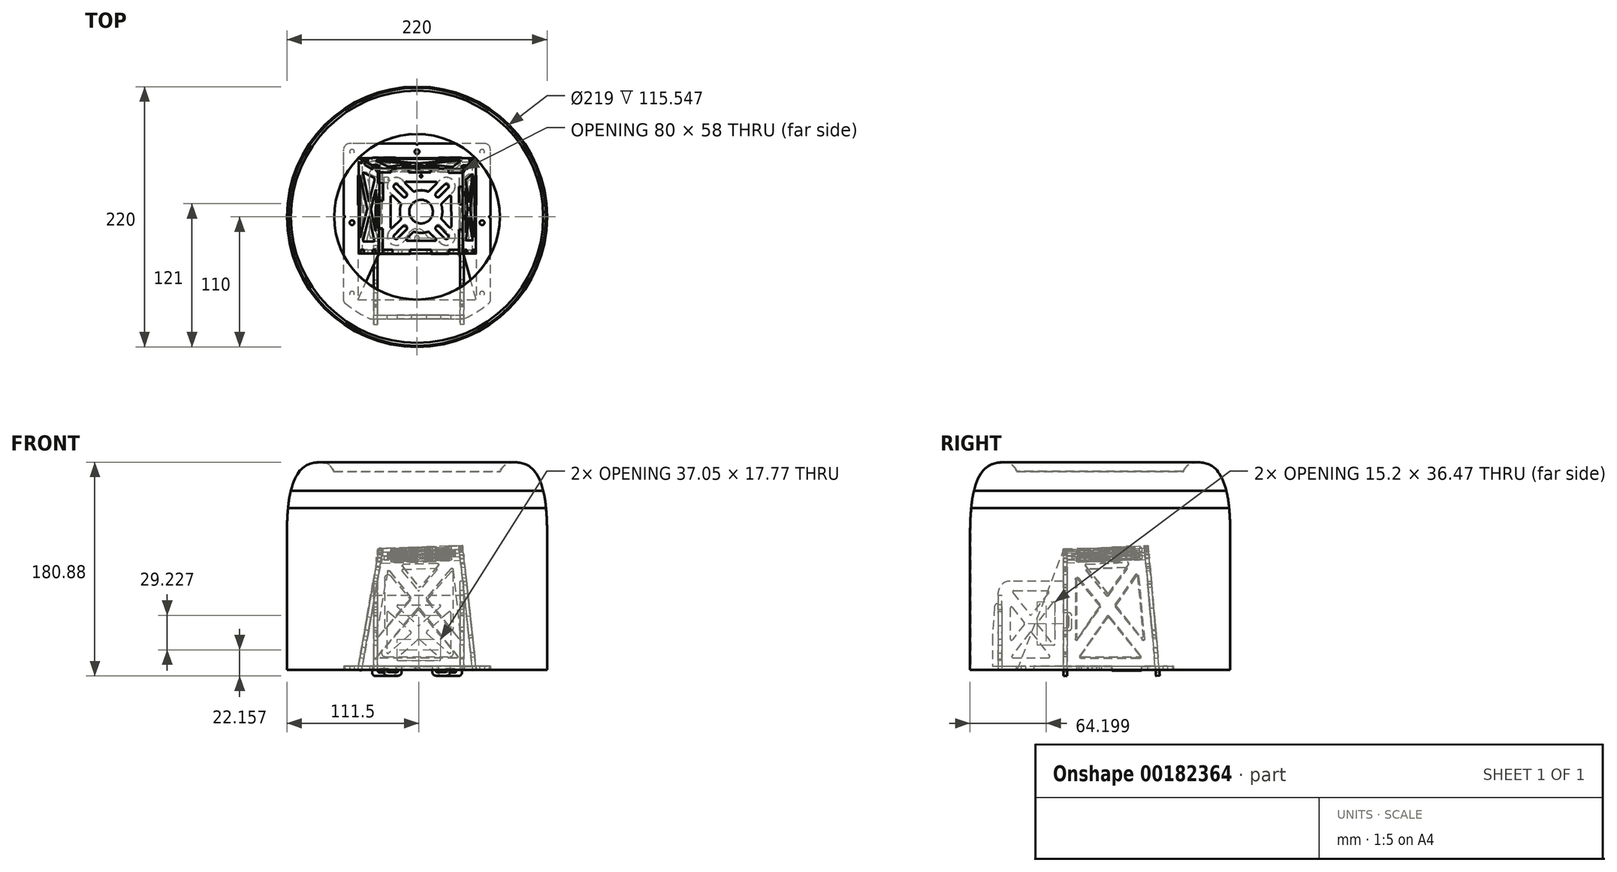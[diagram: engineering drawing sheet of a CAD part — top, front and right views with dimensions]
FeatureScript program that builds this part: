
annotation { "Feature Type Name" : "Feature", "Feature Type Description" : "" }
export const myFeature = defineFeature(function(context is Context, id is Id, definition is map)
    precondition{}
    {
        {
            var Q0;
            Q0=qCreatedBy(makeId("Top.planeOp"),FACE);
            var sketch = newSketch(context, id + "F0", { "sketchPlane" : qUnion([Q0])});
            skLineSegment(sketch, "E0.bottom", {"start": v(-50, 50) * mm, "end": v(50, 50) * mm});
            skLineSegment(sketch, "E0.top", {"start": v(-50, -70) * mm, "end": v(50, -70) * mm});
            skLineSegment(sketch, "E0.left", {"start": v(-50, 50) * mm, "end": v(-50, -70) * mm});
            skLineSegment(sketch, "E0.right", {"start": v(50, 50) * mm, "end": v(50, -70) * mm});
            skSolve(sketch);
        }
        {
            var Q0;
            Q0=qCreatedBy(makeId("Top.planeOp"),FACE);
            cPlane(context, id + "F1", {"entities" : qUnion([Q0]), "cplaneType" : CPlaneType.OFFSET, "offset" : 105 * mm, "width" : 150 * mm, "height" : 150 * mm});
        }
        {
            var Q0;
            Q0=qCreatedBy(id+"F1.planeOp",FACE);
            var sketch = newSketch(context, id + "F2", { "sketchPlane" : qUnion([Q0])});
            skLineSegment(sketch, "E1.bottom", {"start": v(-31.5, 40.5) * mm, "end": v(38.5, 40.5) * mm});
            skLineSegment(sketch, "E1.top", {"start": v(-31.5, -29.5) * mm, "end": v(38.5, -29.5) * mm});
            skLineSegment(sketch, "E1.left", {"start": v(-31.5, 40.5) * mm, "end": v(-31.5, -29.5) * mm});
            skLineSegment(sketch, "E1.right", {"start": v(38.5, 40.5) * mm, "end": v(38.5, -29.5) * mm});
            skSolve(sketch);
        }
        {
            var Q0;
            Q0 = qSketchRegion(id + "F0", true);
            var Q1;
            Q1 = qSketchRegion(id + "F2", true);
            loft(context, id + "F3", {"sheetProfilesArray" : [{ "sheetProfileEntities" : qUnion([Q0]) }, { "sheetProfileEntities" : qUnion([Q1]) }]});
        }
        {
            var Q0;
            Q0=qCreatedBy(id+"F1.planeOp",FACE);
            var sketch = newSketch(context, id + "F4", { "sketchPlane" : qUnion([Q0])});
            skLineSegment(sketch, "E2", {"start": v(-55.6, 40.5) * mm, "end": v(63.29, 40.5) * mm});
            skSolve(sketch);
        }
        {
            var Q0;
            Q0=sQuery(id+"F4.wireOp",EDGE,"E2");
            var Q1;
            Q1=qCreatedBy(id+"F1.planeOp",FACE);
            cPlane(context, id + "F5", {"entities" : qUnion([Q0, Q1]), "cplaneType" : CPlaneType.LINE_ANGLE, "offset" : 25 * mm, "angle" : 2.5 * degree, "width" : 150 * mm, "height" : 150 * mm});
        }
        {
            var Q0;
            Q0=qCreatedBy(id+"F5.planeOp",FACE);
            var sketch = newSketch(context, id + "F6", { "sketchPlane" : qUnion([Q0])});
            skLineSegment(sketch, "E3", {"start": v(38.5, -42.4) * mm, "end": v(38.5, 44.3) * mm});
            skSolve(sketch);
        }
        {
            var Q0;
            Q0=qCreatedBy(id+"F5.planeOp",FACE);
            var Q1;
            Q1=sQuery(id+"F6.wireOp",EDGE,"E3");
            cPlane(context, id + "F7", {"entities" : qUnion([Q0, Q1]), "cplaneType" : CPlaneType.LINE_ANGLE, "offset" : 25 * mm, "angle" : 2 * degree, "width" : 150 * mm, "height" : 150 * mm});
        }
        {
            var Q0;
            Q0=qCreatedBy(id+"F7.planeOp",FACE);
            cPlane(context, id + "F8", {"entities" : qUnion([Q0]), "cplaneType" : CPlaneType.OFFSET, "offset" : 6.2 * mm, "oppositeDirection" : true, "width" : 150 * mm, "height" : 150 * mm});
        }
        {
            var Q0;
            Q0=qCreatedBy(id+"F7.planeOp",FACE);
            var sketch = newSketch(context, id + "F9", { "sketchPlane" : qUnion([Q0])});
            skLineSegment(sketch, "E4", {"start": v(-28.4, 45.16) * mm, "end": v(-28.96, -27.3) * mm});
            skLineSegment(sketch, "E5", {"start": v(42.08, 45.04) * mm, "end": v(-28.4, 45.16) * mm});
            skLineSegment(sketch, "E6", {"start": v(42.42, -26.22) * mm, "end": v(42.08, 45.04) * mm});
            skLineSegment(sketch, "E7", {"start": v(-28.96, -27.3) * mm, "end": v(42.42, -26.22) * mm});
            skSolve(sketch);
        }
        {
            var Q1;
            Q1 = qSketchRegion(id + "F9", true);
            var Q2;
            Q2 = qSketchRegion(id + "F2", true);
            loft(context, id + "F10", {"operationType" : NewBodyOperationType.REMOVE, "sheetProfilesArray" : [{ "sheetProfileEntities" : qUnion([Q1]) }, { "sheetProfileEntities" : qUnion([Q2]) }]});
        }
        {
            var Q0;
            Q0=qCreatedBy(makeId("Top.planeOp"),FACE);
            var sketch = newSketch(context, id + "F11", { "sketchPlane" : qUnion([Q0])});
            skLineSegment(sketch, "E8.0.0", {"start": v(-50, -55) * mm, "end": v(-50, -40) * mm, "construction": true});
            skLineSegment(sketch, "E8.0.1", {"start": v(38, 50) * mm, "end": v(18, 50) * mm});
            skLineSegment(sketch, "E8.0.2", {"start": v(50, -55) * mm, "end": v(50, -40) * mm, "construction": true});
            skLineSegment(sketch, "E9.0", {"start": v(-62, -71.06) * mm, "end": v(-62, -1) * mm});
            skLineSegment(sketch, "E9.2", {"start": v(62, -71.06) * mm, "end": v(62, -1) * mm});
            skLineSegment(sketch, "E9.3", {"start": v(57, 62) * mm, "end": v(1, 62) * mm});
            skLineSegment(sketch, "E10.0", {"start": v(-46.8, -55) * mm, "end": v(-46.8, -40) * mm, "construction": true});
            skLineSegment(sketch, "E10.2", {"start": v(46.8, -55) * mm, "end": v(46.8, -40) * mm, "construction": true});
            skLineSegment(sketch, "E10.3", {"start": v(38, 46.8) * mm, "end": v(18, 46.8) * mm});
            skLineSegment(sketch, "E11.0", {"start": v(-40, -15.5) * mm, "end": v(-40, 37.5) * mm});
            skLineSegment(sketch, "E11.2", {"start": v(40, -15.5) * mm, "end": v(40, 37.5) * mm});
            skLineSegment(sketch, "E11.3", {"start": v(37.5, 40) * mm, "end": v(-37.5, 40) * mm});
            skPoint(sketch, "E12.visualSharp", {"position": v(40, 40) * mm});
            skArc(sketch, "E12.filletArc", {"start": v(40, 37.5) * mm, "mid": v(39.27, 39.27) * mm, "end": v(37.5, 40) * mm});
            skPoint(sketch, "E13.visualSharp", {"position": v(-40, 40) * mm});
            skArc(sketch, "E13.filletArc", {"start": v(-37.5, 40) * mm, "mid": v(-39.27, 39.27) * mm, "end": v(-40, 37.5) * mm});
            skLineSegment(sketch, "E14.0", {"start": v(50, -55) * mm, "end": v(46.8, -55) * mm, "construction": true});
            skLineSegment(sketch, "E15.0", {"start": v(50, -40) * mm, "end": v(46.8, -40) * mm, "construction": true});
            skLineSegment(sketch, "E16.0", {"start": v(50, 35) * mm, "end": v(46.8, 35) * mm});
            skLineSegment(sketch, "E17.0", {"start": v(50, 10) * mm, "end": v(46.8, 10) * mm});
            skLineSegment(sketch, "E18.trimOffspring", {"start": v(-46.8, -40) * mm, "end": v(-50, -40) * mm, "construction": true});
            skLineSegment(sketch, "E19.trimOffspring", {"start": v(-46.8, 35) * mm, "end": v(-50, 35) * mm});
            skLineSegment(sketch, "E20.trimOffspring", {"start": v(-46.8, 10) * mm, "end": v(-50, 10) * mm});
            skLineSegment(sketch, "E21.trimOffspring", {"start": v(-46.8, -55) * mm, "end": v(-50, -55) * mm, "construction": true});
            skLineSegment(sketch, "E22.trimOffspring", {"start": v(-18, 46.8) * mm, "end": v(-18, 50) * mm});
            skLineSegment(sketch, "E23.trimOffspring", {"start": v(-38, 46.8) * mm, "end": v(-38, 50) * mm});
            skLineSegment(sketch, "E24.trimOffspring", {"start": v(18, 46.8) * mm, "end": v(18, 50) * mm});
            skLineSegment(sketch, "E25.trimOffspring", {"start": v(50, 10) * mm, "end": v(50, 35) * mm});
            skLineSegment(sketch, "E26.trimOffspring", {"start": v(46.8, 10) * mm, "end": v(46.8, 35) * mm});
            skLineSegment(sketch, "E27.trimOffspring", {"start": v(38, 46.8) * mm, "end": v(38, 50) * mm});
            skLineSegment(sketch, "E28.trimOffspring", {"start": v(-18, 46.8) * mm, "end": v(-38, 46.8) * mm});
            skLineSegment(sketch, "E29.trimOffspring", {"start": v(-18, 50) * mm, "end": v(-38, 50) * mm});
            skLineSegment(sketch, "E30.trimOffspring", {"start": v(-50, 10) * mm, "end": v(-50, 35) * mm});
            skLineSegment(sketch, "E31.trimOffspring", {"start": v(-46.8, 10) * mm, "end": v(-46.8, 35) * mm});
            skPoint(sketch, "E32.visualSharp", {"position": v(62, 62) * mm});
            skArc(sketch, "E32.filletArc", {"start": v(62, 57) * mm, "mid": v(60.54, 60.54) * mm, "end": v(57, 62) * mm});
            skPoint(sketch, "E33.visualSharp", {"position": v(-62, 62) * mm});
            skArc(sketch, "E33.filletArc", {"start": v(-57, 62) * mm, "mid": v(-60.54, 60.54) * mm, "end": v(-62, 57) * mm});
            skLineSegment(sketch, "E34", {"start": v(-28, -28) * mm, "end": v(-13, -28) * mm});
            skLineSegment(sketch, "E35.0", {"start": v(-37.5, -18) * mm, "end": v(-12, -18) * mm});
            skLineSegment(sketch, "E36", {"start": v(-28, -28) * mm, "end": v(-28, -31.2) * mm});
            skLineSegment(sketch, "E37", {"start": v(-13, -28) * mm, "end": v(-13, -31.2) * mm});
            skLineSegment(sketch, "E38", {"start": v(13, -28) * mm, "end": v(13, -31.2) * mm});
            skLineSegment(sketch, "E39", {"start": v(28, -28) * mm, "end": v(28, -31.2) * mm});
            skLineSegment(sketch, "E40.trimOffspring", {"start": v(13, -28) * mm, "end": v(28, -28) * mm});
            skPoint(sketch, "E41.visualSharp", {"position": v(-40, -18) * mm});
            skArc(sketch, "E41.filletArc", {"start": v(-40, -15.5) * mm, "mid": v(-39.27, -17.27) * mm, "end": v(-37.5, -18) * mm});
            skPoint(sketch, "E42.visualSharp", {"position": v(40, -18) * mm});
            skArc(sketch, "E42.filletArc", {"start": v(37.5, -18) * mm, "mid": v(39.27, -17.27) * mm, "end": v(40, -15.5) * mm});
            skLineSegment(sketch, "E43.top", {"start": v(-28.5, -31.2) * mm, "end": v(-28, -31.2) * mm});
            skLineSegment(sketch, "E43.left", {"start": v(-33.5, -86.2) * mm, "end": v(-33.5, -71.2) * mm});
            skLineSegment(sketch, "E43.right", {"start": v(36.5, -86.2) * mm, "end": v(36.5, -71.2) * mm});
            skPoint(sketch, "E44.visualSharp", {"position": v(-33.5, -31.2) * mm});
            skArc(sketch, "E44.filletArc", {"start": v(-28.5, -31.2) * mm, "mid": v(-32.04, -32.66) * mm, "end": v(-33.5, -36.2) * mm});
            skPoint(sketch, "E45.visualSharp", {"position": v(36.5, -31.2) * mm});
            skArc(sketch, "E45.filletArc", {"start": v(36.5, -36.2) * mm, "mid": v(35.04, -32.66) * mm, "end": v(31.5, -31.2) * mm});
            skLineSegment(sketch, "E46.trimOffspring", {"start": v(-13, -31.2) * mm, "end": v(13, -31.2) * mm});
            skLineSegment(sketch, "E47.trimOffspring", {"start": v(28, -31.2) * mm, "end": v(31.5, -31.2) * mm});
            skLineSegment(sketch, "E48.0", {"start": v(-36.7, -71.2) * mm, "end": v(-36.7, -56.2) * mm});
            skLineSegment(sketch, "E49.0", {"start": v(39.7, -71.2) * mm, "end": v(39.7, -56.2) * mm});
            skLineSegment(sketch, "E50", {"start": v(-36.7, -56.2) * mm, "end": v(-33.5, -56.2) * mm});
            skLineSegment(sketch, "E51", {"start": v(-36.7, -71.2) * mm, "end": v(-33.5, -71.2) * mm});
            skLineSegment(sketch, "E52", {"start": v(36.5, -56.2) * mm, "end": v(39.7, -56.2) * mm});
            skLineSegment(sketch, "E53", {"start": v(36.5, -71.2) * mm, "end": v(39.7, -71.2) * mm});
            skLineSegment(sketch, "E54.trimOffspring", {"start": v(-33.5, -56.2) * mm, "end": v(-33.5, -36.2) * mm});
            skLineSegment(sketch, "E55.trimOffspring", {"start": v(36.5, -56.2) * mm, "end": v(36.5, -36.2) * mm});
            skLineSegment(sketch, "E56", {"start": v(-39.49, -86.2) * mm, "end": v(-33.5, -86.2) * mm});
            skLineSegment(sketch, "E57.trimOffspring", {"start": v(36.5, -86.2) * mm, "end": v(39.49, -86.2) * mm});
            skPoint(sketch, "E58.visualSharp", {"position": v(-62, -86.2) * mm});
            skPoint(sketch, "E59.visualSharp", {"position": v(62, -86.2) * mm});
            skArc(sketch, "E60", {"start": v(40.34, -86.01) * mm, "mid": v(51.26, -79.99) * mm, "end": v(61.3, -72.58) * mm});
            skArc(sketch, "E61.trimOffspring", {"start": v(-61.3, -72.58) * mm, "mid": v(-51.26, -79.99) * mm, "end": v(-40.34, -86.01) * mm});
            skPoint(sketch, "E62.visualSharp", {"position": v(62, -71.98) * mm});
            skArc(sketch, "E62.filletArc", {"start": v(61.3, -72.58) * mm, "mid": v(61.81, -71.9) * mm, "end": v(62, -71.06) * mm});
            skPoint(sketch, "E63.visualSharp", {"position": v(39.93, -86.2) * mm});
            skArc(sketch, "E63.filletArc", {"start": v(39.49, -86.2) * mm, "mid": v(39.92, -86.15) * mm, "end": v(40.34, -86.01) * mm});
            skPoint(sketch, "E64.visualSharp", {"position": v(-39.93, -86.2) * mm});
            skArc(sketch, "E64.filletArc", {"start": v(-40.34, -86.01) * mm, "mid": v(-39.92, -86.15) * mm, "end": v(-39.49, -86.2) * mm});
            skPoint(sketch, "E65.visualSharp", {"position": v(-62, -71.98) * mm});
            skArc(sketch, "E65.filletArc", {"start": v(-62, -71.06) * mm, "mid": v(-61.81, -71.9) * mm, "end": v(-61.3, -72.58) * mm});
            skCircle(sketch, "E66", {"center": v(-55, 55) * mm, "radius": 2 * mm});
            skCircle(sketch, "E67", {"center": v(55, 55) * mm, "radius": 2 * mm});
            skCircle(sketch, "E68", {"center": v(-55, -5) * mm, "radius": 2 * mm});
            skCircle(sketch, "E69", {"center": v(55, -5) * mm, "radius": 2 * mm});
            skCircle(sketch, "E70", {"center": v(-55, -65) * mm, "radius": 2 * mm});
            skCircle(sketch, "E71", {"center": v(55, -65) * mm, "radius": 2 * mm});
            skCircle(sketch, "E72", {"center": v(0, 55) * mm, "radius": 2 * mm});
            skCircle(sketch, "E73", {"center": v(0, -18) * mm, "radius": 2 * mm});
            skPoint(sketch, "E73.centerSnap0", {"position": v(0, -18) * mm});
            skArc(sketch, "E74", {"start": v(-7.38, -14.92) * mm, "mid": v(-4.84, -11.63) * mm, "end": v(-1, -10.06) * mm});
            skLineSegment(sketch, "E75.trimOffspring", {"start": v(12, -18) * mm, "end": v(37.5, -18) * mm});
            skPoint(sketch, "E76.visualSharp", {"position": v(8, -18) * mm});
            skArc(sketch, "E76.filletArc", {"start": v(7.38, -14.92) * mm, "mid": v(9.23, -17.16) * mm, "end": v(12, -18) * mm});
            skPoint(sketch, "E77.visualSharp", {"position": v(-8, -18) * mm});
            skArc(sketch, "E77.filletArc", {"start": v(-12, -18) * mm, "mid": v(-9.23, -17.16) * mm, "end": v(-7.38, -14.92) * mm});
            skLineSegment(sketch, "E78", {"start": v(0, 76.35) * mm, "end": v(0, -96.17) * mm, "construction": true});
            skPoint(sketch, "E78.startSnap0", {"position": v(0, 62) * mm});
            skLineSegment(sketch, "E79", {"start": v(102.81, 0) * mm, "end": v(-83.24, 0) * mm, "construction": true});
            skArc(sketch, "E80", {"start": v(-1, 62) * mm, "mid": v(0, 61) * mm, "end": v(1, 62) * mm});
            skLineSegment(sketch, "E81.trimOffspring", {"start": v(-1, 62) * mm, "end": v(-57, 62) * mm});
            skArc(sketch, "E82", {"start": v(-62, -1) * mm, "mid": v(-61, 0) * mm, "end": v(-62, 1) * mm});
            skLineSegment(sketch, "E83.trimOffspring", {"start": v(-62, 1) * mm, "end": v(-62, 57) * mm});
            skArc(sketch, "E84", {"start": v(62, 1) * mm, "mid": v(61, 0) * mm, "end": v(62, -1) * mm});
            skLineSegment(sketch, "E85.trimOffspring", {"start": v(62, 1) * mm, "end": v(62, 57) * mm});
            skArc(sketch, "E86", {"start": v(-1, -10.06) * mm, "mid": v(0, -11) * mm, "end": v(1, -10.06) * mm});
            skArc(sketch, "E87.trimOffspring", {"start": v(1, -10.06) * mm, "mid": v(4.84, -11.63) * mm, "end": v(7.38, -14.92) * mm});
            skArc(sketch, "E88", {"start": v(1, -10.06) * mm, "mid": v(0, -10) * mm, "end": v(-1, -10.06) * mm, "construction": true});
            skSolve(sketch);
        }
        {
            var Q0;
            Q0 = qSketchRegion(id + "F11", true);
            extrude(context, id + "F12", {"entities" : qUnion([Q0]), "depth" : 3.2 * mm});
        }
        {
            var Q0;
            Q0=sQuery(id+"F11.wireOp",EDGE,"E46.trimOffspring");
            cPlane(context, id + "F13", {"entities" : qUnion([Q0]), "cplaneType" : CPlaneType.LINE_ANGLE, "offset" : 25 * mm, "angle" : 0 * degree, "oppositeDirection" : true, "width" : 150 * mm, "height" : 150 * mm});
        }
        {
            var Q0;
            Q0=qCreatedBy(id+"F8.planeOp",FACE);
            var sketch = newSketch(context, id + "F14", { "sketchPlane" : qUnion([Q0])});
            skLineSegment(sketch, "E89", {"start": v(-3.3, -27.07) * mm, "end": v(11.7, -27.04) * mm});
            skPoint(sketch, "E90.orphan", {"position": v(-30.3, -30.03) * mm});
            skPoint(sketch, "E91.orphan", {"position": v(42.89, -28.92) * mm});
            skLineSegment(sketch, "E92.0", {"start": v(-27.02, -23.87) * mm, "end": v(-3.3, -23.84) * mm});
            skLineSegment(sketch, "E92.1", {"start": v(-26.5, 42.21) * mm, "end": v(-26.68, 20.42) * mm});
            skLineSegment(sketch, "E92.2", {"start": v(39.32, 42.1) * mm, "end": v(13.3, 42.15) * mm});
            skLineSegment(sketch, "E92.3", {"start": v(39.63, -23.77) * mm, "end": v(39.5, 3.31) * mm});
            skLineSegment(sketch, "E93", {"start": v(13.3, 45.88) * mm, "end": v(13.3, 42.15) * mm});
            skLineSegment(sketch, "E94", {"start": v(-30.98, 20.46) * mm, "end": v(-26.68, 20.42) * mm});
            skLineSegment(sketch, "E95", {"start": v(-31.1, 5.46) * mm, "end": v(-26.8, 5.42) * mm});
            skLineSegment(sketch, "E96", {"start": v(42.66, 18.33) * mm, "end": v(39.43, 18.31) * mm});
            skLineSegment(sketch, "E97", {"start": v(42.73, 3.33) * mm, "end": v(39.5, 3.31) * mm});
            skLineSegment(sketch, "E98", {"start": v(-3.3, -27.07) * mm, "end": v(-3.3, -23.84) * mm});
            skLineSegment(sketch, "E99", {"start": v(11.7, -27.04) * mm, "end": v(11.7, -23.81) * mm});
            skLineSegment(sketch, "E100.trimOffspring", {"start": v(-1.7, 42.17) * mm, "end": v(-26.5, 42.21) * mm});
            skLineSegment(sketch, "E101.trimOffspring", {"start": v(-26.8, 5.42) * mm, "end": v(-27.02, -23.87) * mm});
            skLineSegment(sketch, "E102.trimOffspring", {"start": v(11.7, -23.81) * mm, "end": v(39.63, -23.77) * mm});
            skLineSegment(sketch, "E103.trimOffspring", {"start": v(39.43, 18.31) * mm, "end": v(39.32, 42.1) * mm});
            skPoint(sketch, "E104.orphan", {"position": v(42.53, 45.33) * mm});
            skPoint(sketch, "E105.orphan", {"position": v(-29.71, 45.45) * mm});
            skPoint(sketch, "E106.orphan", {"position": v(-30.3, -27.1) * mm});
            skArc(sketch, "E107.0", {"start": v(19.26, 24.85) * mm, "mid": v(19.27, 21.17) * mm, "end": v(22.95, 21.18) * mm});
            skLineSegment(sketch, "E108.0", {"start": v(22.95, 21.18) * mm, "end": v(30, 28.27) * mm});
            skArc(sketch, "E109.0", {"start": v(30, 28.27) * mm, "mid": v(30, 31.94) * mm, "end": v(26.31, 31.94) * mm});
            skLineSegment(sketch, "E110.0", {"start": v(19.26, 24.85) * mm, "end": v(26.31, 31.94) * mm});
            skLineSegment(sketch, "E111.0", {"start": v(-5.35, 24.79) * mm, "end": v(-12.43, 31.84) * mm});
            skLineSegment(sketch, "E112.0", {"start": v(-9.02, 21.1) * mm, "end": v(-16.1, 28.16) * mm});
            skArc(sketch, "E113.0", {"start": v(-12.43, 31.84) * mm, "mid": v(-16.11, 31.83) * mm, "end": v(-16.1, 28.16) * mm});
            skArc(sketch, "E114.0", {"start": v(-9.02, 21.1) * mm, "mid": v(-5.34, 21.11) * mm, "end": v(-5.35, 24.79) * mm});
            skCircle(sketch, "E115.0", {"center": v(7, 8.84) * mm, "radius": 10 * mm});
            skLineSegment(sketch, "E116.0", {"start": v(-5.27, -7.17) * mm, "end": v(-12.32, -14.26) * mm});
            skArc(sketch, "E117.0", {"start": v(-5.27, -7.17) * mm, "mid": v(-5.28, -3.5) * mm, "end": v(-8.96, -3.5) * mm});
            skLineSegment(sketch, "E118.0", {"start": v(-8.96, -3.5) * mm, "end": v(-16, -10.6) * mm});
            skArc(sketch, "E119.0", {"start": v(-16, -10.6) * mm, "mid": v(-16, -14.27) * mm, "end": v(-12.32, -14.26) * mm});
            skArc(sketch, "E120.0", {"start": v(23, -3.43) * mm, "mid": v(19.33, -3.44) * mm, "end": v(19.34, -7.11) * mm});
            skLineSegment(sketch, "E121.0", {"start": v(19.34, -7.11) * mm, "end": v(26.43, -14.17) * mm});
            skLineSegment(sketch, "E122.0", {"start": v(23, -3.43) * mm, "end": v(30.1, -10.48) * mm});
            skArc(sketch, "E123.0", {"start": v(26.43, -14.17) * mm, "mid": v(30.1, -14.16) * mm, "end": v(30.1, -10.48) * mm});
            skLineSegment(sketch, "E124", {"start": v(-14.17, -12.43) * mm, "end": v(28.16, 30.1) * mm, "construction": true});
            skLineSegment(sketch, "E125", {"start": v(-14.27, 30) * mm, "end": v(28.26, -12.33) * mm, "construction": true});
            skCircle(sketch, "E126", {"center": v(7, 8.84) * mm, "radius": 20 * mm, "construction": true});
            skCircle(sketch, "E127", {"center": v(7, 8.84) * mm, "radius": 30 * mm, "construction": true});
            skLineSegment(sketch, "E128.0", {"start": v(-5.28, -14.13) * mm, "end": v(0.32, -8.5) * mm});
            skLineSegment(sketch, "E129.0", {"start": v(-17.16, -4.8) * mm, "end": v(-10.3, 2.08) * mm});
            skLineSegment(sketch, "E130.0", {"start": v(-16.96, 22.1) * mm, "end": v(-10.34, 15.5) * mm});
            skLineSegment(sketch, "E131.0", {"start": v(-6.12, 32.47) * mm, "end": v(0.24, 26.14) * mm});
            skLineSegment(sketch, "E132", {"start": v(-18.67, 21.4) * mm, "end": v(-18.87, -4.09) * mm});
            skLineSegment(sketch, "E133", {"start": v(-5.41, 34.18) * mm, "end": v(19.19, 34.14) * mm});
            skLineSegment(sketch, "E134", {"start": v(32.42, 21.33) * mm, "end": v(32.54, -3.6) * mm});
            skLineSegment(sketch, "E135", {"start": v(-4.57, -15.84) * mm, "end": v(18.7, -15.8) * mm});
            skPoint(sketch, "E136.visualSharp", {"position": v(-3.61, 8.81) * mm});
            skArc(sketch, "E137.filletArc", {"start": v(32.42, 21.33) * mm, "mid": v(31.8, 22.25) * mm, "end": v(30.7, 22.03) * mm});
            skArc(sketch, "E138.filletArc", {"start": v(30.83, -4.3) * mm, "mid": v(31.92, -4.52) * mm, "end": v(32.54, -3.6) * mm});
            skPoint(sketch, "E139.visualSharp", {"position": v(-6.98, -15.84) * mm});
            skArc(sketch, "E139.filletArc", {"start": v(-5.28, -14.13) * mm, "mid": v(-5.5, -15.22) * mm, "end": v(-4.57, -15.84) * mm});
            skArc(sketch, "E140.filletArc", {"start": v(18.7, -15.8) * mm, "mid": v(19.62, -15.18) * mm, "end": v(19.4, -14.1) * mm});
            skPoint(sketch, "E141.visualSharp", {"position": v(-18.88, -6.54) * mm});
            skArc(sketch, "E141.filletArc", {"start": v(-18.87, -4.09) * mm, "mid": v(-18.25, -5.02) * mm, "end": v(-17.16, -4.8) * mm});
            skPoint(sketch, "E142.visualSharp", {"position": v(-18.65, 23.78) * mm});
            skArc(sketch, "E142.filletArc", {"start": v(-16.96, 22.1) * mm, "mid": v(-18.05, 22.32) * mm, "end": v(-18.67, 21.4) * mm});
            skPoint(sketch, "E143.visualSharp", {"position": v(-7.84, 34.18) * mm});
            skArc(sketch, "E143.filletArc", {"start": v(-5.41, 34.18) * mm, "mid": v(-6.34, 33.56) * mm, "end": v(-6.12, 32.47) * mm});
            skArc(sketch, "E144.filletArc", {"start": v(19.9, 32.43) * mm, "mid": v(20.11, 33.52) * mm, "end": v(19.19, 34.14) * mm});
            skArc(sketch, "E145.trimOffspring", {"start": v(12.64, 25.93) * mm, "mid": v(6.95, 26.84) * mm, "end": v(1.26, 25.9) * mm});
            skArc(sketch, "E146.trimOffspring", {"start": v(24.09, 3.19) * mm, "mid": v(25, 8.88) * mm, "end": v(24.06, 14.57) * mm});
            skArc(sketch, "E147.trimOffspring", {"start": v(1.35, -8.25) * mm, "mid": v(7.04, -9.16) * mm, "end": v(12.73, -8.23) * mm});
            skArc(sketch, "E148.trimOffspring", {"start": v(-10.1, 14.48) * mm, "mid": v(-11, 8.8) * mm, "end": v(-10.07, 3.1) * mm});
            skLineSegment(sketch, "E149.trimOffspring", {"start": v(13.75, -8.47) * mm, "end": v(19.4, -14.1) * mm});
            skLineSegment(sketch, "E150.trimOffspring", {"start": v(24.33, 2.17) * mm, "end": v(30.83, -4.3) * mm});
            skLineSegment(sketch, "E151.trimOffspring", {"start": v(24.3, 15.6) * mm, "end": v(30.7, 22.03) * mm});
            skLineSegment(sketch, "E152.trimOffspring", {"start": v(13.67, 26.17) * mm, "end": v(19.9, 32.43) * mm});
            skPoint(sketch, "E153.visualSharp", {"position": v(-9.9, 15.06) * mm});
            skArc(sketch, "E153.filletArc", {"start": v(-10.1, 14.48) * mm, "mid": v(-10.07, 15.03) * mm, "end": v(-10.34, 15.5) * mm});
            skArc(sketch, "E154.filletArc", {"start": v(-10.3, 2.08) * mm, "mid": v(-10.04, 2.56) * mm, "end": v(-10.07, 3.1) * mm});
            skPoint(sketch, "E155.visualSharp", {"position": v(0.69, 25.7) * mm});
            skArc(sketch, "E155.filletArc", {"start": v(0.24, 26.14) * mm, "mid": v(0.72, 25.87) * mm, "end": v(1.26, 25.9) * mm});
            skPoint(sketch, "E156.visualSharp", {"position": v(13.22, 25.73) * mm});
            skArc(sketch, "E156.filletArc", {"start": v(12.64, 25.93) * mm, "mid": v(13.19, 25.9) * mm, "end": v(13.67, 26.17) * mm});
            skPoint(sketch, "E157.visualSharp", {"position": v(23.85, 15.14) * mm});
            skArc(sketch, "E157.filletArc", {"start": v(24.3, 15.6) * mm, "mid": v(24.03, 15.11) * mm, "end": v(24.06, 14.57) * mm});
            skPoint(sketch, "E158.visualSharp", {"position": v(23.88, 2.61) * mm});
            skArc(sketch, "E158.filletArc", {"start": v(24.09, 3.19) * mm, "mid": v(24.06, 2.64) * mm, "end": v(24.33, 2.17) * mm});
            skPoint(sketch, "E159.visualSharp", {"position": v(13.3, -8.02) * mm});
            skArc(sketch, "E159.filletArc", {"start": v(13.75, -8.47) * mm, "mid": v(13.27, -8.2) * mm, "end": v(12.73, -8.23) * mm});
            skPoint(sketch, "E160.visualSharp", {"position": v(0.77, -8.05) * mm});
            skArc(sketch, "E160.filletArc", {"start": v(1.35, -8.25) * mm, "mid": v(0.8, -8.23) * mm, "end": v(0.32, -8.5) * mm});
            skLineSegment(sketch, "E161.0", {"start": v(-30.98, 20.46) * mm, "end": v(-31.1, 5.46) * mm});
            skLineSegment(sketch, "E162.0", {"start": v(13.3, 45.88) * mm, "end": v(-1.7, 45.9) * mm});
            skLineSegment(sketch, "E163.0", {"start": v(43.3, 3.33) * mm, "end": v(43.23, 18.33) * mm});
            skLineSegment(sketch, "E164", {"start": v(42.66, 18.33) * mm, "end": v(43.23, 18.33) * mm});
            skLineSegment(sketch, "E165", {"start": v(42.73, 3.33) * mm, "end": v(43.3, 3.33) * mm});
            skLineSegment(sketch, "E166", {"start": v(42.89, -28.92) * mm, "end": v(42.53, 45.33) * mm, "construction": true});
            skLineSegment(sketch, "E167", {"start": v(42.53, 45.33) * mm, "end": v(-29.71, 45.45) * mm, "construction": true});
            skLineSegment(sketch, "E168", {"start": v(-1.7, 42.17) * mm, "end": v(-1.7, 45.9) * mm});
            skLineSegment(sketch, "E169", {"start": v(-29.71, 45.45) * mm, "end": v(-30.3, -30.03) * mm, "construction": true});
            skCircle(sketch, "E170", {"center": v(7, 38.84) * mm, "radius": 1 * mm});
            skText(sketch, "E171", { "text": "B", "fontName": "OpenSans-Bold.ttf"});
            const initialGuessF14  = {"E171": [-0.02505, 0.03283, 1, 0, 0.00506]};
            skSetInitialGuess(sketch, initialGuessF14);
            skSolve(sketch);
        }
        {
            var Q0;
            Q0 = qSketchRegion(id + "F14", true);
            extrude(context, id + "F15", {"entities" : qUnion([Q0]), "oppositeDirection" : true, "depth" : 3.2 * mm});
        }
        {
            var Q0;
            Q0=qCreatedBy(id+"F13.planeOp",FACE);
            var sketch = newSketch(context, id + "F16", { "sketchPlane" : qUnion([Q0])});
            skLineSegment(sketch, "E172", {"start": v(-40.47, 86.97) * mm, "end": v(-42.1, 72.06) * mm});
            skLineSegment(sketch, "E173", {"start": v(29.22, 99.5) * mm, "end": v(20.85, 99.8) * mm});
            skLineSegment(sketch, "E174.0", {"start": v(28, 3.2) * mm, "end": v(28, 0) * mm});
            skLineSegment(sketch, "E175.0", {"start": v(13, 3.2) * mm, "end": v(13, 0) * mm});
            skLineSegment(sketch, "E176.0", {"start": v(-13, 3.2) * mm, "end": v(-13, 0) * mm});
            skLineSegment(sketch, "E177.0", {"start": v(-28, 3.2) * mm, "end": v(-28, 0) * mm});
            skLineSegment(sketch, "E178.0", {"start": v(13, 3.2) * mm, "end": v(-13, 3.2) * mm});
            skLineSegment(sketch, "E179", {"start": v(46.19, 3.2) * mm, "end": v(28, 3.2) * mm});
            skLineSegment(sketch, "E180", {"start": v(-28, 3.2) * mm, "end": v(-31.5, 3.2) * mm});
            skLineSegment(sketch, "E181", {"start": v(-31.5, 3.2) * mm, "end": v(-46.43, 3.2) * mm});
            skPoint(sketch, "E182.0.end.orphan", {"position": v(-28, 3.2) * mm});
            skPoint(sketch, "E182.0.start.orphan", {"position": v(-13, 3.2) * mm});
            skPoint(sketch, "E183.0.end.orphan", {"position": v(13, 3.2) * mm});
            skPoint(sketch, "E183.0.start.orphan", {"position": v(28, 3.2) * mm});
            skPoint(sketch, "E184.end.orphan", {"position": v(-62, 3.2) * mm});
            skPoint(sketch, "E185.orphan", {"position": v(50, 0) * mm});
            skPoint(sketch, "E186.start.orphan", {"position": v(62, 3.2) * mm});
            skPoint(sketch, "E187.orphan", {"position": v(-50, 0) * mm});
            skLineSegment(sketch, "E188.0", {"start": v(-35.98, 98.58) * mm, "end": v(-37.3, 86.62) * mm});
            skLineSegment(sketch, "E188.1", {"start": v(20.73, 96.6) * mm, "end": v(5.74, 97.12) * mm});
            skLineSegment(sketch, "E189.0", {"start": v(46.19, 3.2) * mm, "end": v(44.45, 13.05) * mm});
            skLineSegment(sketch, "E190", {"start": v(20.85, 99.8) * mm, "end": v(20.73, 96.6) * mm});
            skLineSegment(sketch, "E191", {"start": v(5.85, 100.32) * mm, "end": v(5.74, 97.12) * mm});
            skLineSegment(sketch, "E192", {"start": v(-11.86, 100.94) * mm, "end": v(-11.97, 97.74) * mm});
            skLineSegment(sketch, "E193", {"start": v(-26.85, 101.46) * mm, "end": v(-26.96, 98.26) * mm});
            skLineSegment(sketch, "E194.trimOffspring", {"start": v(5.85, 100.32) * mm, "end": v(-11.86, 100.94) * mm});
            skLineSegment(sketch, "E195.trimOffspring", {"start": v(-11.97, 97.74) * mm, "end": v(-26.96, 98.26) * mm});
            skLineSegment(sketch, "E196.trimOffspring", {"start": v(-26.85, 101.46) * mm, "end": v(-35.63, 101.77) * mm});
            skLineSegment(sketch, "E197", {"start": v(35.1, 84.62) * mm, "end": v(31.94, 84.06) * mm});
            skLineSegment(sketch, "E198", {"start": v(37.7, 69.84) * mm, "end": v(34.54, 69.29) * mm});
            skLineSegment(sketch, "E199", {"start": v(45, 28.38) * mm, "end": v(41.85, 27.82) * mm});
            skLineSegment(sketch, "E200", {"start": v(47.6, 13.6) * mm, "end": v(44.45, 13.05) * mm});
            skLineSegment(sketch, "E201.trimOffspring", {"start": v(31.94, 84.06) * mm, "end": v(31.94, 84.06) * mm});
            skLineSegment(sketch, "E202.trimOffspring", {"start": v(41.85, 27.82) * mm, "end": v(34.54, 69.29) * mm});
            skPoint(sketch, "E203.orphan", {"position": v(46.8, 3.2) * mm});
            skLineSegment(sketch, "E204", {"start": v(31.94, 84.06) * mm, "end": v(29.22, 99.5) * mm});
            skPoint(sketch, "E205.orphan", {"position": v(32.49, 99.39) * mm});
            skLineSegment(sketch, "E206", {"start": v(-40.47, 86.97) * mm, "end": v(-37.3, 86.62) * mm});
            skLineSegment(sketch, "E207", {"start": v(-42.1, 72.06) * mm, "end": v(-38.93, 71.71) * mm});
            skLineSegment(sketch, "E208", {"start": v(-46.73, 29.82) * mm, "end": v(-43.55, 29.47) * mm});
            skLineSegment(sketch, "E209", {"start": v(-48.37, 14.91) * mm, "end": v(-45.19, 14.56) * mm});
            skPoint(sketch, "E210.orphan", {"position": v(-38.84, 101.88) * mm});
            skLineSegment(sketch, "E211.trimOffspring", {"start": v(-46.73, 29.82) * mm, "end": v(-48.37, 14.91) * mm});
            skLineSegment(sketch, "E212.trimOffspring", {"start": v(-38.93, 71.71) * mm, "end": v(-43.55, 29.47) * mm});
            skLineSegment(sketch, "E213.trimOffspring", {"start": v(-45.19, 14.56) * mm, "end": v(-46.43, 3.2) * mm});
            skPoint(sketch, "E214.end.orphan", {"position": v(-49.65, 3.2) * mm});
            skPoint(sketch, "E215.orphan", {"position": v(-46.8, 3.2) * mm});
            skLineSegment(sketch, "E216", {"start": v(-35.98, 98.58) * mm, "end": v(-35.63, 101.77) * mm});
            skLineSegment(sketch, "E217", {"start": v(47.6, 13.6) * mm, "end": v(45, 28.38) * mm});
            skLineSegment(sketch, "E218.trimOffspring", {"start": v(37.7, 69.84) * mm, "end": v(35.1, 84.62) * mm});
            skLineSegment(sketch, "E219", {"start": v(33.5, 3.2) * mm, "end": v(33.5, 66.89) * mm, "construction": true});
            skLineSegment(sketch, "E220", {"start": v(-36.5, 3.2) * mm, "end": v(-36.5, 34.63) * mm, "construction": true});
            skLineSegment(sketch, "E221.bottom", {"start": v(33.5, 48.2) * mm, "end": v(36.7, 48.2) * mm});
            skLineSegment(sketch, "E221.top", {"start": v(33.5, 33.2) * mm, "end": v(36.7, 33.2) * mm});
            skLineSegment(sketch, "E221.left", {"start": v(33.5, 48.2) * mm, "end": v(33.5, 33.2) * mm});
            skLineSegment(sketch, "E221.right", {"start": v(36.7, 48.2) * mm, "end": v(36.7, 33.2) * mm});
            skLineSegment(sketch, "E222.bottom", {"start": v(-36.5, 48.2) * mm, "end": v(-39.7, 48.2) * mm});
            skLineSegment(sketch, "E222.top", {"start": v(-36.5, 33.2) * mm, "end": v(-39.7, 33.2) * mm});
            skLineSegment(sketch, "E222.left", {"start": v(-36.5, 48.2) * mm, "end": v(-36.5, 33.2) * mm});
            skLineSegment(sketch, "E222.right", {"start": v(-39.7, 48.2) * mm, "end": v(-39.7, 33.2) * mm});
            skLineSegment(sketch, "E223", {"start": v(32.49, 99.39) * mm, "end": v(-50, 0) * mm, "construction": true});
            skLineSegment(sketch, "E224", {"start": v(-38.84, 101.88) * mm, "end": v(50, 0) * mm, "construction": true});
            skLineSegment(sketch, "E225", {"start": v(27.5, 77.24) * mm, "end": v(27.5, 36.08) * mm});
            skLineSegment(sketch, "E226", {"start": v(11.87, 84.9) * mm, "end": v(-16.02, 85.87) * mm});
            skLineSegment(sketch, "E227", {"start": v(-30.5, 82.04) * mm, "end": v(-30.5, 34.1) * mm});
            skLineSegment(sketch, "E228.trimOffspring", {"start": v(27, 11.2) * mm, "end": v(-27.82, 11.2) * mm});
            skLineSegment(sketch, "E229.trimOffspring", {"start": v(22.2, 79.15) * mm, "end": v(5.87, 59.49) * mm});
            skLineSegment(sketch, "E230.trimOffspring", {"start": v(12.6, 83.26) * mm, "end": v(-0.58, 67.38) * mm});
            skLineSegment(sketch, "E231.trimOffspring", {"start": v(-16.8, 84.22) * mm, "end": v(-2.1, 67.36) * mm});
            skLineSegment(sketch, "E232.trimOffspring", {"start": v(-28.75, 82.7) * mm, "end": v(-8.36, 59.32) * mm});
            skLineSegment(sketch, "E233.trimOffspring", {"start": v(-8.34, 58.02) * mm, "end": v(-28.73, 33.46) * mm});
            skLineSegment(sketch, "E234.trimOffspring", {"start": v(-1.9, 50.14) * mm, "end": v(-30.13, 16.12) * mm});
            skLineSegment(sketch, "E235.trimOffspring", {"start": v(-0.37, 50.15) * mm, "end": v(29.26, 16.17) * mm});
            skLineSegment(sketch, "E236.trimOffspring", {"start": v(5.89, 58.2) * mm, "end": v(25.75, 35.42) * mm});
            skPoint(sketch, "E237.visualSharp", {"position": v(13.9, 84.83) * mm});
            skArc(sketch, "E237.filletArc", {"start": v(12.6, 83.26) * mm, "mid": v(12.75, 84.3) * mm, "end": v(11.87, 84.9) * mm});
            skPoint(sketch, "E238.visualSharp", {"position": v(-1.33, 66.47) * mm});
            skArc(sketch, "E238.filletArc", {"start": v(-2.1, 67.36) * mm, "mid": v(-1.34, 67.01) * mm, "end": v(-0.58, 67.38) * mm});
            skPoint(sketch, "E239.visualSharp", {"position": v(-7.8, 58.68) * mm});
            skArc(sketch, "E239.filletArc", {"start": v(-8.34, 58.02) * mm, "mid": v(-8.11, 58.67) * mm, "end": v(-8.36, 59.32) * mm});
            skPoint(sketch, "E240.visualSharp", {"position": v(-30.5, 84.7) * mm});
            skArc(sketch, "E240.filletArc", {"start": v(-28.75, 82.7) * mm, "mid": v(-29.85, 82.98) * mm, "end": v(-30.5, 82.04) * mm});
            skPoint(sketch, "E241.visualSharp", {"position": v(-30.5, 31.32) * mm});
            skArc(sketch, "E241.filletArc", {"start": v(-30.5, 34.1) * mm, "mid": v(-29.84, 33.15) * mm, "end": v(-28.73, 33.46) * mm});
            skPoint(sketch, "E242.visualSharp", {"position": v(-1.14, 51.04) * mm});
            skArc(sketch, "E242.filletArc", {"start": v(-0.37, 50.15) * mm, "mid": v(-1.13, 50.5) * mm, "end": v(-1.9, 50.14) * mm});
            skPoint(sketch, "E243.visualSharp", {"position": v(27.5, 18.2) * mm});
            skPoint(sketch, "E244.visualSharp", {"position": v(27.5, 33.41) * mm});
            skArc(sketch, "E244.filletArc", {"start": v(25.75, 35.42) * mm, "mid": v(26.85, 35.14) * mm, "end": v(27.5, 36.08) * mm});
            skPoint(sketch, "E245.visualSharp", {"position": v(5.33, 58.84) * mm});
            skArc(sketch, "E245.filletArc", {"start": v(5.87, 59.49) * mm, "mid": v(5.64, 58.84) * mm, "end": v(5.89, 58.2) * mm});
            skPoint(sketch, "E246.visualSharp", {"position": v(27.5, 85.55) * mm});
            skArc(sketch, "E246.filletArc", {"start": v(27.5, 77.24) * mm, "mid": v(25.52, 80.06) * mm, "end": v(22.2, 79.15) * mm});
            skPoint(sketch, "E247.visualSharp", {"position": v(-18.32, 85.95) * mm});
            skArc(sketch, "E247.filletArc", {"start": v(-16.02, 85.87) * mm, "mid": v(-16.95, 85.3) * mm, "end": v(-16.8, 84.22) * mm});
            skLineSegment(sketch, "E248.0", {"start": v(6.62, 94.08) * mm, "end": v(-8.37, 94.6) * mm});
            skLineSegment(sketch, "E249.0", {"start": v(6.51, 90.88) * mm, "end": v(-8.48, 91.4) * mm});
            skLineSegment(sketch, "E250", {"start": v(6.62, 94.08) * mm, "end": v(6.51, 90.88) * mm});
            skLineSegment(sketch, "E251", {"start": v(-8.37, 94.6) * mm, "end": v(-8.48, 91.4) * mm});
            skPoint(sketch, "E252.left.start.orphan", {"position": v(33.5, 38.2) * mm});
            skArc(sketch, "E253.filletArc", {"start": v(-30.13, 16.12) * mm, "mid": v(-30.53, 12.92) * mm, "end": v(-27.82, 11.2) * mm});
            skPoint(sketch, "E254.visualSharp", {"position": v(33.6, 11.2) * mm});
            skArc(sketch, "E254.filletArc", {"start": v(27, 11.2) * mm, "mid": v(29.73, 12.96) * mm, "end": v(29.26, 16.17) * mm});
            skPoint(sketch, "E255.start.orphan", {"position": v(28.5, 3.2) * mm});
            skLineSegment(sketch, "E256.top", {"start": v(25, -5) * mm, "end": v(16, -5) * mm});
            skLineSegment(sketch, "E256.left", {"start": v(28, 0) * mm, "end": v(28, -2) * mm});
            skLineSegment(sketch, "E256.right", {"start": v(13, 0) * mm, "end": v(13, -2) * mm});
            skLineSegment(sketch, "E257.top", {"start": v(-25, -5) * mm, "end": v(-16, -5) * mm});
            skLineSegment(sketch, "E257.left", {"start": v(-28, 0) * mm, "end": v(-28, -2) * mm});
            skLineSegment(sketch, "E257.right", {"start": v(-13, 0) * mm, "end": v(-13, -2) * mm});
            skPoint(sketch, "E258.visualSharp", {"position": v(28, -5) * mm});
            skArc(sketch, "E258.filletArc", {"start": v(25, -5) * mm, "mid": v(27.12, -4.12) * mm, "end": v(28, -2) * mm});
            skPoint(sketch, "E259.visualSharp", {"position": v(13, -5) * mm});
            skArc(sketch, "E259.filletArc", {"start": v(13, -2) * mm, "mid": v(13.88, -4.12) * mm, "end": v(16, -5) * mm});
            skPoint(sketch, "E260.visualSharp", {"position": v(-13, -5) * mm});
            skArc(sketch, "E260.filletArc", {"start": v(-16, -5) * mm, "mid": v(-13.88, -4.12) * mm, "end": v(-13, -2) * mm});
            skPoint(sketch, "E261.visualSharp", {"position": v(-28, -5) * mm});
            skArc(sketch, "E261.filletArc", {"start": v(-28, -2) * mm, "mid": v(-27.12, -4.12) * mm, "end": v(-25, -5) * mm});
            skLineSegment(sketch, "E262.bottom", {"start": v(24, 0.5) * mm, "end": v(17, 0.5) * mm});
            skLineSegment(sketch, "E262.top", {"start": v(24, -2) * mm, "end": v(17, -2) * mm});
            skLineSegment(sketch, "E262.left", {"start": v(25, -0.5) * mm, "end": v(25, -1) * mm});
            skLineSegment(sketch, "E262.right", {"start": v(16, -0.5) * mm, "end": v(16, -1) * mm});
            skArc(sketch, "E263.filletArc", {"start": v(16, -1) * mm, "mid": v(16.3, -1.7) * mm, "end": v(17, -2) * mm});
            skArc(sketch, "E264.filletArc", {"start": v(24, -2) * mm, "mid": v(24.7, -1.7) * mm, "end": v(25, -1) * mm});
            skPoint(sketch, "E265.visualSharp", {"position": v(25, 0) * mm});
            skArc(sketch, "E265.filletArc", {"start": v(25, -0.5) * mm, "mid": v(24.7, 0.2) * mm, "end": v(24, 0.5) * mm});
            skPoint(sketch, "E266.visualSharp", {"position": v(16, 0.5) * mm});
            skArc(sketch, "E266.filletArc", {"start": v(17, 0.5) * mm, "mid": v(16.3, 0.2) * mm, "end": v(16, -0.5) * mm});
            skLineSegment(sketch, "E267.bottom", {"start": v(-17, 0.5) * mm, "end": v(-24, 0.5) * mm});
            skLineSegment(sketch, "E267.top", {"start": v(-17, -2) * mm, "end": v(-24, -2) * mm});
            skLineSegment(sketch, "E267.left", {"start": v(-16, -0.5) * mm, "end": v(-16, -1) * mm});
            skLineSegment(sketch, "E267.right", {"start": v(-25, -0.5) * mm, "end": v(-25, -1) * mm});
            skPoint(sketch, "E268.visualSharp", {"position": v(-16, 0) * mm});
            skArc(sketch, "E268.filletArc", {"start": v(-16, -0.5) * mm, "mid": v(-16.3, 0.2) * mm, "end": v(-17, 0.5) * mm});
            skArc(sketch, "E269.filletArc", {"start": v(-17, -2) * mm, "mid": v(-16.3, -1.7) * mm, "end": v(-16, -1) * mm});
            skPoint(sketch, "E270.visualSharp", {"position": v(-25, 0.5) * mm});
            skArc(sketch, "E270.filletArc", {"start": v(-24, 0.5) * mm, "mid": v(-24.7, 0.2) * mm, "end": v(-25, -0.5) * mm});
            skArc(sketch, "E271.filletArc", {"start": v(-25, -1) * mm, "mid": v(-24.7, -1.7) * mm, "end": v(-24, -2) * mm});
            skSolve(sketch);
        }
        {
            var Q0;
            Q0 = qSketchRegion(id + "F16", true);
            extrude(context, id + "F17", {"entities" : qUnion([Q0]), "depth" : 3.2 * mm});
        }
        {
            var Q0;
            Q0=makeQuery(id+"F3.opLoft","SWEPT_FACE",FACE,{"disambiguationData":[OSD([sQuery(id+"F0.wireOp",EDGE,"E0.bottom"),sQuery(id+"F0.wireOp",EDGE,"E0.top"),sQuery(id+"F0.wireOp",EDGE,"E0.left"),sQuery(id+"F2.wireOp",EDGE,"E1.bottom"),sQuery(id+"F2.wireOp",EDGE,"E1.top"),sQuery(id+"F2.wireOp",EDGE,"E1.left")])]});
            var sketch = newSketch(context, id + "F18", { "sketchPlane" : qUnion([Q0])});
            skLineSegment(sketch, "E272.0", {"start": v(-35, -8.68) * mm, "end": v(-10, -8.68) * mm});
            skPoint(sketch, "E273.0", {"position": v(-35, -8.68) * mm});
            skPoint(sketch, "E274.0", {"position": v(-10, -8.68) * mm});
            skPoint(sketch, "E275.0", {"position": v(40, -8.68) * mm});
            skPoint(sketch, "E276.0", {"position": v(55, -8.68) * mm});
            skLineSegment(sketch, "E277", {"start": v(31.2, -5.43) * mm, "end": v(-10, -5.43) * mm});
            skLineSegment(sketch, "E278", {"start": v(-35, -5.43) * mm, "end": v(-46.5, -5.43) * mm});
            skPoint(sketch, "E279.orphan", {"position": v(-62, -5.43) * mm});
            skPoint(sketch, "E280.orphan", {"position": v(82, -10.97) * mm});
            skLineSegment(sketch, "E281", {"start": v(-10, -8.68) * mm, "end": v(-10, -5.43) * mm});
            skLineSegment(sketch, "E282", {"start": v(-35, -8.68) * mm, "end": v(-35, -5.43) * mm});
            skPoint(sketch, "E283.orphan", {"position": v(-50, -8.68) * mm});
            skPoint(sketch, "E284.orphan", {"position": v(70, -8.68) * mm});
            skLineSegment(sketch, "E285.1", {"start": v(-37.8, 92.12) * mm, "end": v(-28.88, 91.72) * mm});
            skLineSegment(sketch, "E285.2", {"start": v(-46.5, -5.43) * mm, "end": v(-45.08, 10.5) * mm});
            skLineSegment(sketch, "E286", {"start": v(-28.73, 94.92) * mm, "end": v(-28.88, 91.72) * mm});
            skLineSegment(sketch, "E287", {"start": v(-13.75, 94.25) * mm, "end": v(-13.9, 91.05) * mm});
            skLineSegment(sketch, "E288", {"start": v(9.9, 93.2) * mm, "end": v(9.76, 90) * mm});
            skLineSegment(sketch, "E289.trimOffspring", {"start": v(-13.9, 91.05) * mm, "end": v(9.76, 90) * mm});
            skLineSegment(sketch, "E290", {"start": v(-42.05, 80.51) * mm, "end": v(-38.87, 80.23) * mm});
            skLineSegment(sketch, "E291", {"start": v(-43.38, 65.57) * mm, "end": v(-40.2, 65.29) * mm});
            skLineSegment(sketch, "E292", {"start": v(-47.43, 25.77) * mm, "end": v(-43.75, 25.44) * mm});
            skLineSegment(sketch, "E293.trimOffspring", {"start": v(-38.87, 80.23) * mm, "end": v(-37.8, 92.12) * mm});
            skPoint(sketch, "E294.orphan", {"position": v(-40.72, 95.45) * mm});
            skLineSegment(sketch, "E295.trimOffspring", {"start": v(-43.75, 25.44) * mm, "end": v(-40.2, 65.29) * mm});
            skPoint(sketch, "E296.orphan", {"position": v(-49.49, -5.43) * mm});
            skPoint(sketch, "E297.orphan", {"position": v(31.67, 92.22) * mm});
            skLineSegment(sketch, "E298.0", {"start": v(28, 62.24) * mm, "end": v(28, 77.24) * mm});
            skLineSegment(sketch, "E299.0", {"start": v(28, 77.24) * mm, "end": v(31.2, 77.24) * mm});
            skLineSegment(sketch, "E300.0", {"start": v(28, 62.24) * mm, "end": v(31.2, 62.24) * mm});
            skLineSegment(sketch, "E301.0", {"start": v(28, 5.14) * mm, "end": v(28, 20.14) * mm});
            skLineSegment(sketch, "E302.0", {"start": v(28, 20.14) * mm, "end": v(31.2, 20.14) * mm});
            skLineSegment(sketch, "E303.0", {"start": v(28, 5.14) * mm, "end": v(31.2, 5.14) * mm});
            skPoint(sketch, "E304.orphan", {"position": v(31.2, 92.92) * mm});
            skPoint(sketch, "E305.orphan", {"position": v(31.2, 77.24) * mm});
            skLineSegment(sketch, "E306", {"start": v(31.2, 92.92) * mm, "end": v(-50, -8.68) * mm, "construction": true});
            skLineSegment(sketch, "E307", {"start": v(31.2, -8.68) * mm, "end": v(-40.72, 95.45) * mm, "construction": true});
            skLineSegment(sketch, "E308.0", {"start": v(19.22, 69.92) * mm, "end": v(0.25, 46.19) * mm});
            skLineSegment(sketch, "E309.0", {"start": v(19.18, 17.53) * mm, "end": v(0.2, 45) * mm});
            skLineSegment(sketch, "E310", {"start": v(-32.6, 71.77) * mm, "end": v(-37.38, 18.06) * mm});
            skLineSegment(sketch, "E311", {"start": v(-21.6, 79.38) * mm, "end": v(10.79, 77.94) * mm});
            skLineSegment(sketch, "E312", {"start": v(21, 69.3) * mm, "end": v(21, 18.1) * mm});
            skLineSegment(sketch, "E313", {"start": v(-33.33, 1.57) * mm, "end": v(16.14, 1.57) * mm});
            skLineSegment(sketch, "E314.trimOffspring", {"start": v(11.53, 76.32) * mm, "end": v(-5.31, 55.25) * mm});
            skLineSegment(sketch, "E315.trimOffspring", {"start": v(16.96, 3.14) * mm, "end": v(-5.97, 36.34) * mm});
            skLineSegment(sketch, "E316.trimOffspring", {"start": v(-13.1, 46.65) * mm, "end": v(-30.77, 72.25) * mm});
            skLineSegment(sketch, "E317.trimOffspring", {"start": v(-7.58, 36.4) * mm, "end": v(-34.1, 3.2) * mm});
            skLineSegment(sketch, "E318.trimOffspring", {"start": v(-6.92, 55.3) * mm, "end": v(-22.46, 77.82) * mm});
            skLineSegment(sketch, "E319.trimOffspring", {"start": v(-13.13, 45.46) * mm, "end": v(-35.6, 17.35) * mm});
            skPoint(sketch, "E320.visualSharp", {"position": v(-32.35, 74.53) * mm});
            skArc(sketch, "E320.filletArc", {"start": v(-30.77, 72.25) * mm, "mid": v(-31.85, 72.65) * mm, "end": v(-32.6, 71.77) * mm});
            skPoint(sketch, "E321.visualSharp", {"position": v(-37.67, 14.76) * mm});
            skArc(sketch, "E321.filletArc", {"start": v(-37.38, 18.06) * mm, "mid": v(-36.75, 17.05) * mm, "end": v(-35.6, 17.35) * mm});
            skPoint(sketch, "E322.visualSharp", {"position": v(-12.67, 46.04) * mm});
            skArc(sketch, "E322.filletArc", {"start": v(-13.13, 45.46) * mm, "mid": v(-12.92, 46.05) * mm, "end": v(-13.1, 46.65) * mm});
            skPoint(sketch, "E323.visualSharp", {"position": v(-6.15, 54.2) * mm});
            skArc(sketch, "E323.filletArc", {"start": v(-6.92, 55.3) * mm, "mid": v(-6.13, 54.87) * mm, "end": v(-5.31, 55.25) * mm});
            skPoint(sketch, "E324.visualSharp", {"position": v(12.75, 77.85) * mm});
            skArc(sketch, "E324.filletArc", {"start": v(11.53, 76.32) * mm, "mid": v(11.66, 77.35) * mm, "end": v(10.79, 77.94) * mm});
            skPoint(sketch, "E325.visualSharp", {"position": v(-23.6, 79.47) * mm});
            skArc(sketch, "E325.filletArc", {"start": v(-21.6, 79.38) * mm, "mid": v(-22.52, 78.87) * mm, "end": v(-22.46, 77.82) * mm});
            skPoint(sketch, "E326.visualSharp", {"position": v(21, 72.15) * mm});
            skArc(sketch, "E326.filletArc", {"start": v(21, 69.3) * mm, "mid": v(20.33, 70.24) * mm, "end": v(19.22, 69.92) * mm});
            skPoint(sketch, "E327.visualSharp", {"position": v(21, 14.89) * mm});
            skArc(sketch, "E327.filletArc", {"start": v(19.18, 17.53) * mm, "mid": v(20.3, 17.14) * mm, "end": v(21, 18.1) * mm});
            skPoint(sketch, "E328.visualSharp", {"position": v(-0.22, 45.6) * mm});
            skArc(sketch, "E328.filletArc", {"start": v(0.25, 46.19) * mm, "mid": v(0.03, 45.6) * mm, "end": v(0.2, 45) * mm});
            skPoint(sketch, "E329.visualSharp", {"position": v(-6.74, 37.45) * mm});
            skArc(sketch, "E329.filletArc", {"start": v(-5.97, 36.34) * mm, "mid": v(-6.76, 36.77) * mm, "end": v(-7.58, 36.4) * mm});
            skPoint(sketch, "E330.visualSharp", {"position": v(18.04, 1.57) * mm});
            skArc(sketch, "E330.filletArc", {"start": v(16.14, 1.57) * mm, "mid": v(17.02, 2.1) * mm, "end": v(16.96, 3.14) * mm});
            skPoint(sketch, "E331.visualSharp", {"position": v(-35.4, 1.57) * mm});
            skArc(sketch, "E331.filletArc", {"start": v(-34.1, 3.2) * mm, "mid": v(-34.23, 2.14) * mm, "end": v(-33.33, 1.57) * mm});
            skLineSegment(sketch, "E332", {"start": v(-1.32, 87.35) * mm, "end": v(-16.3, 88.02) * mm});
            skLineSegment(sketch, "E333.0", {"start": v(-16.45, 84.82) * mm, "end": v(-1.47, 84.15) * mm});
            skLineSegment(sketch, "E334", {"start": v(-1.32, 87.35) * mm, "end": v(-1.47, 84.15) * mm});
            skLineSegment(sketch, "E335", {"start": v(-16.3, 88.02) * mm, "end": v(-16.45, 84.82) * mm});
            skLineSegment(sketch, "E336.0", {"start": v(31.2, 77.24) * mm, "end": v(31.2, 92.24) * mm});
            skPoint(sketch, "E337.visualSharp", {"position": v(75, 2.57) * mm});
            skPoint(sketch, "E338.visualSharp", {"position": v(38.2, 1.57) * mm});
            skPoint(sketch, "E339.visualSharp", {"position": v(38.2, 40.88) * mm});
            skPoint(sketch, "E340.visualSharp", {"position": v(67.05, 1.57) * mm});
            skLineSegment(sketch, "E341", {"start": v(31.67, 92.22) * mm, "end": v(31.2, 92.24) * mm, "construction": true});
            skLineSegment(sketch, "E342.trimOffspring", {"start": v(-28.73, 94.92) * mm, "end": v(-40.72, 95.45) * mm, "construction": true});
            skLineSegment(sketch, "E343.0", {"start": v(-28.68, 96.02) * mm, "end": v(-13.7, 95.35) * mm});
            skLineSegment(sketch, "E344", {"start": v(-28.73, 94.92) * mm, "end": v(-28.68, 96.02) * mm});
            skLineSegment(sketch, "E345", {"start": v(-13.75, 94.25) * mm, "end": v(-13.7, 95.35) * mm});
            skLineSegment(sketch, "E346", {"start": v(-40.72, 95.45) * mm, "end": v(-42.05, 80.51) * mm, "construction": true});
            skLineSegment(sketch, "E347.trimOffspring", {"start": v(9.9, 93.2) * mm, "end": v(-13.75, 94.25) * mm, "construction": true});
            skLineSegment(sketch, "E348.0", {"start": v(9.96, 94.3) * mm, "end": v(31.2, 93.34) * mm});
            skLineSegment(sketch, "E349", {"start": v(9.9, 93.2) * mm, "end": v(9.96, 94.3) * mm});
            skLineSegment(sketch, "E350", {"start": v(31.2, 92.24) * mm, "end": v(31.2, 93.34) * mm});
            skLineSegment(sketch, "E351.trimOffspring", {"start": v(-43.38, 65.57) * mm, "end": v(-47.8, 15.96) * mm, "construction": true});
            skLineSegment(sketch, "E352.0", {"start": v(-43.88, 65.61) * mm, "end": v(-42.55, 80.56) * mm});
            skLineSegment(sketch, "E353", {"start": v(-42.05, 80.51) * mm, "end": v(-42.55, 80.56) * mm});
            skLineSegment(sketch, "E354", {"start": v(-43.38, 65.57) * mm, "end": v(-43.88, 65.61) * mm});
            skLineSegment(sketch, "E355.trimOffspring", {"start": v(-49.14, 1.02) * mm, "end": v(-50, -8.68) * mm, "construction": true});
            skLineSegment(sketch, "E356.0", {"start": v(-48.76, 10.83) * mm, "end": v(-47.43, 25.77) * mm});
            skLineSegment(sketch, "E357", {"start": v(-45.08, 10.5) * mm, "end": v(-48.76, 10.83) * mm});
            skLineSegment(sketch, "E358", {"start": v(31.2, 62.24) * mm, "end": v(31.2, 20.14) * mm});
            skLineSegment(sketch, "E359", {"start": v(31.2, 5.14) * mm, "end": v(31.2, -5.43) * mm});
            skSolve(sketch);
        }
        {
            var Q0;
            Q0 = qSketchRegion(id + "F18", true);
            extrude(context, id + "F19", {"entities" : qUnion([Q0]), "oppositeDirection" : true, "depth" : 3.2 * mm});
        }
        {
            var Q0;
            Q0=makeQuery(id+"F3.opLoft","SWEPT_FACE",FACE,{"disambiguationData":[OSD([sQuery(id+"F0.wireOp",EDGE,"E0.bottom"),sQuery(id+"F0.wireOp",EDGE,"E0.top"),sQuery(id+"F0.wireOp",EDGE,"E0.right"),sQuery(id+"F2.wireOp",EDGE,"E1.bottom"),sQuery(id+"F2.wireOp",EDGE,"E1.top"),sQuery(id+"F2.wireOp",EDGE,"E1.right")])]});
            var sketch = newSketch(context, id + "F20", { "sketchPlane" : qUnion([Q0])});
            skLineSegment(sketch, "E360.0", {"start": v(-28, 82.05) * mm, "end": v(-28, 67.05) * mm});
            skLineSegment(sketch, "E361.0", {"start": v(-28, 82.05) * mm, "end": v(-31.2, 82.05) * mm});
            skLineSegment(sketch, "E362.0", {"start": v(-28, 67.05) * mm, "end": v(-31.2, 67.05) * mm});
            skLineSegment(sketch, "E363.0", {"start": v(-28, 24.56) * mm, "end": v(-31.2, 24.56) * mm});
            skLineSegment(sketch, "E364.0", {"start": v(-28, 24.56) * mm, "end": v(-28, 9.56) * mm});
            skLineSegment(sketch, "E365.0", {"start": v(-28, 9.56) * mm, "end": v(-31.2, 9.56) * mm});
            skLineSegment(sketch, "E366", {"start": v(10, -2.22) * mm, "end": v(-31.2, -2.22) * mm});
            skLineSegment(sketch, "E367", {"start": v(46.5, -2.22) * mm, "end": v(35, -2.22) * mm});
            skLineSegment(sketch, "E368", {"start": v(35, -5.44) * mm, "end": v(10, -5.44) * mm});
            skLineSegment(sketch, "E369", {"start": v(10, -2.22) * mm, "end": v(10, -5.44) * mm});
            skLineSegment(sketch, "E370", {"start": v(35, -2.22) * mm, "end": v(35, -5.44) * mm});
            skPoint(sketch, "E371.orphan", {"position": v(35, -5.44) * mm});
            skPoint(sketch, "E372.orphan", {"position": v(62, -2.22) * mm});
            skPoint(sketch, "E373.end.orphan", {"position": v(50, -5.44) * mm});
            skPoint(sketch, "E373.start.orphan", {"position": v(62, -5.44) * mm});
            skPoint(sketch, "E374.orphan", {"position": v(-70, -5.44) * mm});
            skLineSegment(sketch, "E375.0", {"start": v(46.5, -2.22) * mm, "end": v(45.47, 9.2) * mm});
            skLineSegment(sketch, "E375.1", {"start": v(-10.46, 94.75) * mm, "end": v(10.67, 95.68) * mm});
            skLineSegment(sketch, "E376", {"start": v(-10.6, 97.95) * mm, "end": v(-10.46, 94.75) * mm});
            skLineSegment(sketch, "E377", {"start": v(10.53, 98.87) * mm, "end": v(10.67, 95.68) * mm});
            skLineSegment(sketch, "E378", {"start": v(25.51, 99.53) * mm, "end": v(25.65, 96.33) * mm});
            skLineSegment(sketch, "E379.trimOffspring", {"start": v(25.65, 96.33) * mm, "end": v(37.59, 96.85) * mm});
            skLineSegment(sketch, "E380", {"start": v(41.84, 85.24) * mm, "end": v(38.66, 84.96) * mm});
            skLineSegment(sketch, "E381", {"start": v(43.19, 70.3) * mm, "end": v(40, 70.02) * mm});
            skLineSegment(sketch, "E382", {"start": v(47.31, 24.44) * mm, "end": v(44.13, 24.15) * mm});
            skLineSegment(sketch, "E383", {"start": v(48.66, 9.5) * mm, "end": v(45.47, 9.2) * mm});
            skLineSegment(sketch, "E384.trimOffspring", {"start": v(38.66, 84.96) * mm, "end": v(37.59, 96.85) * mm});
            skPoint(sketch, "E385.orphan", {"position": v(40.5, 100.18) * mm});
            skLineSegment(sketch, "E386.trimOffspring", {"start": v(44.13, 24.15) * mm, "end": v(40, 70.02) * mm});
            skLineSegment(sketch, "E387", {"start": v(-31.2, 97.07) * mm, "end": v(50, -5.44) * mm, "construction": true});
            skLineSegment(sketch, "E388", {"start": v(40.5, 100.18) * mm, "end": v(-31.2, -5.44) * mm, "construction": true});
            skLineSegment(sketch, "E389.0", {"start": v(-18.22, 72.62) * mm, "end": v(-0.38, 50.1) * mm});
            skLineSegment(sketch, "E390", {"start": v(-11.71, 84.69) * mm, "end": v(23.04, 86.2) * mm});
            skLineSegment(sketch, "E391", {"start": v(-20, 72) * mm, "end": v(-20, 23.21) * mm});
            skLineSegment(sketch, "E392", {"start": v(-15.65, 5.78) * mm, "end": v(32.67, 5.78) * mm});
            skLineSegment(sketch, "E393", {"start": v(31.53, 74.9) * mm, "end": v(36.2, 23) * mm});
            skLineSegment(sketch, "E394.trimOffspring", {"start": v(29.7, 75.38) * mm, "end": v(12.88, 50.6) * mm});
            skLineSegment(sketch, "E395.trimOffspring", {"start": v(23.91, 84.65) * mm, "end": v(7.32, 60.2) * mm});
            skLineSegment(sketch, "E396.trimOffspring", {"start": v(7.43, 40.25) * mm, "end": v(33.45, 7.4) * mm});
            skLineSegment(sketch, "E397.trimOffspring", {"start": v(12.93, 49.41) * mm, "end": v(34.42, 22.28) * mm});
            skLineSegment(sketch, "E398.trimOffspring", {"start": v(-0.34, 48.93) * mm, "end": v(-18.17, 22.65) * mm});
            skLineSegment(sketch, "E399.trimOffspring", {"start": v(5.82, 40.19) * mm, "end": v(-16.48, 7.34) * mm});
            skLineSegment(sketch, "E400.trimOffspring", {"start": v(-12.45, 83.07) * mm, "end": v(5.7, 60.14) * mm});
            skPoint(sketch, "E401.visualSharp", {"position": v(0.07, 49.53) * mm});
            skArc(sketch, "E401.filletArc", {"start": v(-0.34, 48.93) * mm, "mid": v(-0.17, 49.52) * mm, "end": v(-0.38, 50.1) * mm});
            skPoint(sketch, "E402.visualSharp", {"position": v(6.55, 59.07) * mm});
            skArc(sketch, "E402.filletArc", {"start": v(5.7, 60.14) * mm, "mid": v(6.53, 59.76) * mm, "end": v(7.32, 60.2) * mm});
            skPoint(sketch, "E403.visualSharp", {"position": v(-20, 74.88) * mm});
            skArc(sketch, "E403.filletArc", {"start": v(-18.22, 72.62) * mm, "mid": v(-19.33, 72.95) * mm, "end": v(-20, 72) * mm});
            skPoint(sketch, "E404.visualSharp", {"position": v(-20, 19.96) * mm});
            skArc(sketch, "E404.filletArc", {"start": v(-20, 23.21) * mm, "mid": v(-19.3, 22.26) * mm, "end": v(-18.17, 22.65) * mm});
            skPoint(sketch, "E405.visualSharp", {"position": v(-13.67, 84.6) * mm});
            skArc(sketch, "E405.filletArc", {"start": v(-11.71, 84.69) * mm, "mid": v(-12.58, 84.1) * mm, "end": v(-12.45, 83.07) * mm});
            skPoint(sketch, "E406.visualSharp", {"position": v(25.03, 86.3) * mm});
            skArc(sketch, "E406.filletArc", {"start": v(23.91, 84.65) * mm, "mid": v(23.96, 85.7) * mm, "end": v(23.04, 86.2) * mm});
            skPoint(sketch, "E407.visualSharp", {"position": v(31.28, 77.7) * mm});
            skArc(sketch, "E407.filletArc", {"start": v(31.53, 74.9) * mm, "mid": v(30.78, 75.78) * mm, "end": v(29.7, 75.38) * mm});
            skPoint(sketch, "E408.visualSharp", {"position": v(36.5, 19.66) * mm});
            skArc(sketch, "E408.filletArc", {"start": v(34.42, 22.28) * mm, "mid": v(35.57, 21.97) * mm, "end": v(36.2, 23) * mm});
            skPoint(sketch, "E409.visualSharp", {"position": v(12.47, 49.99) * mm});
            skArc(sketch, "E409.filletArc", {"start": v(12.88, 50.6) * mm, "mid": v(12.71, 50) * mm, "end": v(12.93, 49.41) * mm});
            skPoint(sketch, "E410.visualSharp", {"position": v(6.58, 41.32) * mm});
            skArc(sketch, "E410.filletArc", {"start": v(7.43, 40.25) * mm, "mid": v(6.6, 40.63) * mm, "end": v(5.82, 40.19) * mm});
            skPoint(sketch, "E411.visualSharp", {"position": v(34.73, 5.78) * mm});
            skArc(sketch, "E411.filletArc", {"start": v(32.67, 5.78) * mm, "mid": v(33.57, 6.34) * mm, "end": v(33.45, 7.4) * mm});
            skPoint(sketch, "E412.visualSharp", {"position": v(-17.54, 5.78) * mm});
            skArc(sketch, "E412.filletArc", {"start": v(-16.48, 7.34) * mm, "mid": v(-16.54, 6.3) * mm, "end": v(-15.65, 5.78) * mm});
            skLineSegment(sketch, "E413.0", {"start": v(-0.9, 92.15) * mm, "end": v(14.08, 92.8) * mm});
            skLineSegment(sketch, "E414.0", {"start": v(-0.76, 88.94) * mm, "end": v(14.22, 89.6) * mm});
            skLineSegment(sketch, "E415", {"start": v(-31.2, 82.05) * mm, "end": v(-31.2, 97.05) * mm});
            skPoint(sketch, "E416.orphan", {"position": v(-30.7, 97.07) * mm});
            skLineSegment(sketch, "E417", {"start": v(-0.76, 88.94) * mm, "end": v(-0.9, 92.15) * mm});
            skLineSegment(sketch, "E418", {"start": v(14.08, 92.8) * mm, "end": v(14.22, 89.6) * mm});
            skLineSegment(sketch, "E419.0", {"start": v(-31.2, 97.55) * mm, "end": v(-10.62, 98.45) * mm});
            skLineSegment(sketch, "E420", {"start": v(-10.6, 97.95) * mm, "end": v(-10.62, 98.45) * mm});
            skLineSegment(sketch, "E421", {"start": v(-31.2, 97.05) * mm, "end": v(-31.2, 97.55) * mm});
            skLineSegment(sketch, "E422", {"start": v(40.5, 100.18) * mm, "end": v(25.51, 99.53) * mm, "construction": true});
            skLineSegment(sketch, "E423.trimOffspring", {"start": v(-30.7, 97.07) * mm, "end": v(-31.2, 97.05) * mm, "construction": true});
            skLineSegment(sketch, "E424.trimOffspring", {"start": v(10.53, 98.87) * mm, "end": v(-10.6, 97.95) * mm, "construction": true});
            skLineSegment(sketch, "E425.0", {"start": v(10.5, 99.37) * mm, "end": v(25.5, 100.03) * mm});
            skLineSegment(sketch, "E426", {"start": v(10.53, 98.87) * mm, "end": v(10.5, 99.37) * mm});
            skLineSegment(sketch, "E427", {"start": v(25.51, 99.53) * mm, "end": v(25.5, 100.03) * mm});
            skLineSegment(sketch, "E428", {"start": v(50, -5.44) * mm, "end": v(48.66, 9.5) * mm, "construction": true});
            skLineSegment(sketch, "E429.trimOffspring", {"start": v(41.84, 85.24) * mm, "end": v(40.5, 100.18) * mm, "construction": true});
            skLineSegment(sketch, "E430.0", {"start": v(43.49, 70.33) * mm, "end": v(42.14, 85.27) * mm});
            skLineSegment(sketch, "E431", {"start": v(41.84, 85.24) * mm, "end": v(42.14, 85.27) * mm});
            skLineSegment(sketch, "E432", {"start": v(43.19, 70.3) * mm, "end": v(43.49, 70.33) * mm});
            skLineSegment(sketch, "E433.trimOffspring", {"start": v(47.31, 24.44) * mm, "end": v(43.19, 70.3) * mm, "construction": true});
            skLineSegment(sketch, "E434.0", {"start": v(48.96, 9.52) * mm, "end": v(47.61, 24.46) * mm});
            skLineSegment(sketch, "E435", {"start": v(47.61, 24.46) * mm, "end": v(47.31, 24.44) * mm});
            skLineSegment(sketch, "E436", {"start": v(48.66, 9.5) * mm, "end": v(48.96, 9.52) * mm});
            skLineSegment(sketch, "E437", {"start": v(-31.2, 67.05) * mm, "end": v(-31.2, 24.56) * mm});
            skLineSegment(sketch, "E438", {"start": v(-31.2, 9.56) * mm, "end": v(-31.2, -2.22) * mm});
            skSolve(sketch);
        }
        {
            var Q0;
            Q0 = qSketchRegion(id + "F20", true);
            extrude(context, id + "F21", {"entities" : qUnion([Q0]), "oppositeDirection" : true, "depth" : 3.2 * mm});
        }
        {
            var Q0;
            Q0=makeQuery(id+"F3.opLoft","SWEPT_FACE",FACE,{"disambiguationData":[OSD([sQuery(id+"F0.wireOp",EDGE,"E0.bottom"),sQuery(id+"F0.wireOp",EDGE,"E0.left"),sQuery(id+"F0.wireOp",EDGE,"E0.right"),sQuery(id+"F2.wireOp",EDGE,"E1.bottom"),sQuery(id+"F2.wireOp",EDGE,"E1.left"),sQuery(id+"F2.wireOp",EDGE,"E1.right")])]});
            var sketch = newSketch(context, id + "F22", { "sketchPlane" : qUnion([Q0])});
            skLineSegment(sketch, "E439", {"start": v(18, -1.3) * mm, "end": v(-18, -1.3) * mm});
            skLineSegment(sketch, "E440", {"start": v(-38, -1.3) * mm, "end": v(-49.65, -1.3) * mm});
            skLineSegment(sketch, "E441", {"start": v(49.44, -1.3) * mm, "end": v(38, -1.3) * mm});
            skLineSegment(sketch, "E442", {"start": v(18, -1.3) * mm, "end": v(18, -4.5) * mm});
            skLineSegment(sketch, "E443", {"start": v(38, -1.3) * mm, "end": v(38, -4.53) * mm});
            skLineSegment(sketch, "E444", {"start": v(-38, -1.3) * mm, "end": v(-38, -4.5) * mm});
            skLineSegment(sketch, "E445", {"start": v(-18, -1.3) * mm, "end": v(-18, -4.5) * mm});
            skPoint(sketch, "E446.end.orphan", {"position": v(-62, -4.5) * mm});
            skPoint(sketch, "E446.start.orphan", {"position": v(-50, -4.5) * mm});
            skPoint(sketch, "E447.orphan", {"position": v(-62, -1.3) * mm});
            skPoint(sketch, "E448.orphan", {"position": v(38, -4.5) * mm});
            skPoint(sketch, "E449.start.orphan", {"position": v(62, -4.5) * mm});
            skPoint(sketch, "E450.orphan", {"position": v(50, -4.5) * mm});
            skPoint(sketch, "E451.orphan", {"position": v(62, -1.3) * mm});
            skLineSegment(sketch, "E452.0", {"start": v(-26.62, 97.3) * mm, "end": v(-11.63, 96.78) * mm});
            skLineSegment(sketch, "E453", {"start": v(-26.5, 100.5) * mm, "end": v(-26.62, 97.3) * mm});
            skLineSegment(sketch, "E454", {"start": v(-11.52, 99.98) * mm, "end": v(-11.63, 96.78) * mm});
            skLineSegment(sketch, "E455", {"start": v(6.95, 99.33) * mm, "end": v(6.84, 96.14) * mm});
            skLineSegment(sketch, "E456", {"start": v(21.94, 98.81) * mm, "end": v(21.83, 95.61) * mm});
            skLineSegment(sketch, "E457.trimOffspring", {"start": v(6.84, 96.14) * mm, "end": v(21.83, 95.61) * mm});
            skLineSegment(sketch, "E458", {"start": v(31.93, 98.46) * mm, "end": v(-50, -4.5) * mm, "construction": true});
            skLineSegment(sketch, "E459", {"start": v(-38.5, 100.92) * mm, "end": v(50, -4.5) * mm, "construction": true});
            skLineSegment(sketch, "E460", {"start": v(-30.42, 80.9) * mm, "end": v(-36.72, 23.18) * mm});
            skLineSegment(sketch, "E461", {"start": v(-17.24, 85.97) * mm, "end": v(11.49, 84.97) * mm});
            skLineSegment(sketch, "E462", {"start": v(24.99, 79.03) * mm, "end": v(34.54, 24.6) * mm});
            skLineSegment(sketch, "E463", {"start": v(-33.4, 5.7) * mm, "end": v(32.75, 5.7) * mm});
            skLineSegment(sketch, "E464.trimOffspring", {"start": v(5.65, 56.1) * mm, "end": v(32.79, 23.78) * mm});
            skLineSegment(sketch, "E465.trimOffspring", {"start": v(-8.3, 55.93) * mm, "end": v(-34.94, 22.45) * mm});
            skLineSegment(sketch, "E466.trimOffspring", {"start": v(-2, 47.8) * mm, "end": v(-34.2, 7.33) * mm});
            skLineSegment(sketch, "E467.trimOffspring", {"start": v(-0.45, 47.81) * mm, "end": v(33.52, 7.35) * mm});
            skLineSegment(sketch, "E468.trimOffspring", {"start": v(23.22, 79.48) * mm, "end": v(5.63, 57.38) * mm});
            skLineSegment(sketch, "E469.trimOffspring", {"start": v(12.24, 83.35) * mm, "end": v(-1.33, 66.3) * mm});
            skLineSegment(sketch, "E470.trimOffspring", {"start": v(-18.04, 84.33) * mm, "end": v(-2.88, 66.27) * mm});
            skLineSegment(sketch, "E471.trimOffspring", {"start": v(-28.66, 81.43) * mm, "end": v(-8.32, 57.2) * mm});
            skPoint(sketch, "E472.visualSharp", {"position": v(-30.17, 83.22) * mm});
            skArc(sketch, "E472.filletArc", {"start": v(-28.66, 81.43) * mm, "mid": v(-29.72, 81.74) * mm, "end": v(-30.42, 80.9) * mm});
            skPoint(sketch, "E473.visualSharp", {"position": v(-37.1, 19.74) * mm});
            skArc(sketch, "E473.filletArc", {"start": v(-36.72, 23.18) * mm, "mid": v(-36.1, 22.15) * mm, "end": v(-34.94, 22.45) * mm});
            skPoint(sketch, "E474.visualSharp", {"position": v(-7.8, 56.57) * mm});
            skArc(sketch, "E474.filletArc", {"start": v(-8.3, 55.93) * mm, "mid": v(-8.09, 56.56) * mm, "end": v(-8.32, 57.2) * mm});
            skPoint(sketch, "E475.visualSharp", {"position": v(-35.48, 5.7) * mm});
            skArc(sketch, "E475.filletArc", {"start": v(-34.2, 7.33) * mm, "mid": v(-34.31, 6.27) * mm, "end": v(-33.4, 5.7) * mm});
            skPoint(sketch, "E476.visualSharp", {"position": v(-1.23, 48.75) * mm});
            skArc(sketch, "E476.filletArc", {"start": v(-0.45, 47.81) * mm, "mid": v(-1.23, 48.17) * mm, "end": v(-2, 47.8) * mm});
            skPoint(sketch, "E477.visualSharp", {"position": v(35.18, 20.92) * mm});
            skArc(sketch, "E477.filletArc", {"start": v(32.79, 23.78) * mm, "mid": v(33.98, 23.51) * mm, "end": v(34.54, 24.6) * mm});
            skPoint(sketch, "E478.visualSharp", {"position": v(5.12, 56.74) * mm});
            skArc(sketch, "E478.filletArc", {"start": v(5.63, 57.38) * mm, "mid": v(5.41, 56.74) * mm, "end": v(5.65, 56.1) * mm});
            skPoint(sketch, "E479.visualSharp", {"position": v(24.6, 81.22) * mm});
            skArc(sketch, "E479.filletArc", {"start": v(24.99, 79.03) * mm, "mid": v(24.25, 79.83) * mm, "end": v(23.22, 79.48) * mm});
            skPoint(sketch, "E480.visualSharp", {"position": v(34.9, 5.7) * mm});
            skArc(sketch, "E480.filletArc", {"start": v(32.75, 5.7) * mm, "mid": v(33.66, 6.29) * mm, "end": v(33.52, 7.35) * mm});
            skPoint(sketch, "E481.visualSharp", {"position": v(13.47, 84.9) * mm});
            skArc(sketch, "E481.filletArc", {"start": v(12.24, 83.35) * mm, "mid": v(12.36, 84.39) * mm, "end": v(11.49, 84.97) * mm});
            skPoint(sketch, "E482.visualSharp", {"position": v(-2.1, 65.33) * mm});
            skArc(sketch, "E482.filletArc", {"start": v(-2.88, 66.27) * mm, "mid": v(-2.1, 65.91) * mm, "end": v(-1.33, 66.3) * mm});
            skPoint(sketch, "E483.visualSharp", {"position": v(-19.49, 86.05) * mm});
            skArc(sketch, "E483.filletArc", {"start": v(-17.24, 85.97) * mm, "mid": v(-18.18, 85.41) * mm, "end": v(-18.04, 84.33) * mm});
            skPoint(sketch, "E484.end.orphan", {"position": v(-18, -4.5) * mm});
            skLineSegment(sketch, "E485.top", {"start": v(-35, -9.5) * mm, "end": v(-21, -9.5) * mm});
            skLineSegment(sketch, "E485.left", {"start": v(-38, -4.5) * mm, "end": v(-38, -6.5) * mm});
            skLineSegment(sketch, "E485.right", {"start": v(-18, -4.5) * mm, "end": v(-18, -6.5) * mm});
            skPoint(sketch, "E486.visualSharp", {"position": v(-38, -9.5) * mm});
            skArc(sketch, "E486.filletArc", {"start": v(-38, -6.5) * mm, "mid": v(-37.12, -8.63) * mm, "end": v(-35, -9.5) * mm});
            skPoint(sketch, "E487.visualSharp", {"position": v(-18, -9.5) * mm});
            skArc(sketch, "E487.filletArc", {"start": v(-21, -9.5) * mm, "mid": v(-18.88, -8.63) * mm, "end": v(-18, -6.5) * mm});
            skLineSegment(sketch, "E488.bottom", {"start": v(-32, -3.76) * mm, "end": v(-24, -3.76) * mm});
            skLineSegment(sketch, "E488.top", {"start": v(-32, -6.5) * mm, "end": v(-24, -6.5) * mm});
            skLineSegment(sketch, "E488.left", {"start": v(-33, -4.76) * mm, "end": v(-33, -5.5) * mm});
            skLineSegment(sketch, "E488.right", {"start": v(-23, -4.76) * mm, "end": v(-23, -5.5) * mm});
            skPoint(sketch, "E489.visualSharp", {"position": v(-33, -6.5) * mm});
            skArc(sketch, "E489.filletArc", {"start": v(-33, -5.5) * mm, "mid": v(-32.7, -6.21) * mm, "end": v(-32, -6.5) * mm});
            skArc(sketch, "E490.filletArc", {"start": v(-24, -6.5) * mm, "mid": v(-23.3, -6.21) * mm, "end": v(-23, -5.5) * mm});
            skPoint(sketch, "E491.visualSharp", {"position": v(-21, -3.76) * mm});
            skArc(sketch, "E491.filletArc", {"start": v(-23, -4.76) * mm, "mid": v(-23.3, -4.05) * mm, "end": v(-24, -3.76) * mm});
            skPoint(sketch, "E492.visualSharp", {"position": v(-35, -4.5) * mm});
            skArc(sketch, "E492.filletArc", {"start": v(-32, -3.76) * mm, "mid": v(-32.7, -4.05) * mm, "end": v(-33, -4.76) * mm});
            skLineSegment(sketch, "E493.top", {"start": v(21, -9.5) * mm, "end": v(35, -9.5) * mm});
            skLineSegment(sketch, "E493.left", {"start": v(18, -4.5) * mm, "end": v(18, -6.5) * mm});
            skLineSegment(sketch, "E493.right", {"start": v(38, -4.5) * mm, "end": v(38, -6.5) * mm});
            skPoint(sketch, "E494.visualSharp", {"position": v(18, -9.5) * mm});
            skArc(sketch, "E494.filletArc", {"start": v(18, -6.5) * mm, "mid": v(18.88, -8.63) * mm, "end": v(21, -9.5) * mm});
            skPoint(sketch, "E495.visualSharp", {"position": v(38, -9.5) * mm});
            skArc(sketch, "E495.filletArc", {"start": v(35, -9.5) * mm, "mid": v(37.12, -8.63) * mm, "end": v(38, -6.5) * mm});
            skLineSegment(sketch, "E496.bottom", {"start": v(24, -3.76) * mm, "end": v(32, -3.76) * mm});
            skLineSegment(sketch, "E496.top", {"start": v(24, -6.5) * mm, "end": v(32, -6.5) * mm});
            skLineSegment(sketch, "E496.left", {"start": v(23, -4.76) * mm, "end": v(23, -5.5) * mm});
            skLineSegment(sketch, "E496.right", {"start": v(33, -4.76) * mm, "end": v(33, -5.5) * mm});
            skPoint(sketch, "E497.visualSharp", {"position": v(23, -6.5) * mm});
            skArc(sketch, "E497.filletArc", {"start": v(23, -5.5) * mm, "mid": v(23.3, -6.21) * mm, "end": v(24, -6.5) * mm});
            skArc(sketch, "E498.filletArc", {"start": v(32, -6.5) * mm, "mid": v(32.7, -6.21) * mm, "end": v(33, -5.5) * mm});
            skArc(sketch, "E499.filletArc", {"start": v(33, -4.76) * mm, "mid": v(32.7, -4.05) * mm, "end": v(32, -3.76) * mm});
            skPoint(sketch, "E500.visualSharp", {"position": v(21, -3.76) * mm});
            skArc(sketch, "E500.filletArc", {"start": v(24, -3.76) * mm, "mid": v(23.3, -4.05) * mm, "end": v(23, -4.76) * mm});
            skLineSegment(sketch, "E501.0.1", {"start": v(-38.5, 100.92) * mm, "end": v(-48.37, 10.4) * mm, "construction": true});
            skLineSegment(sketch, "E501.0.3", {"start": v(49.44, -1.3) * mm, "end": v(44.03, 29.51) * mm, "construction": true});
            skPoint(sketch, "E502.orphan", {"position": v(-9.95, 93.72) * mm});
            skLineSegment(sketch, "E503", {"start": v(-10.07, 90.51) * mm, "end": v(-9.95, 93.72) * mm});
            skLineSegment(sketch, "E504", {"start": v(5.04, 93.2) * mm, "end": v(4.92, 89.99) * mm});
            skLineSegment(sketch, "E505", {"start": v(-9.95, 93.72) * mm, "end": v(5.04, 93.2) * mm});
            skLineSegment(sketch, "E506", {"start": v(-10.07, 90.51) * mm, "end": v(4.92, 89.99) * mm});
            skLineSegment(sketch, "E507.0", {"start": v(-40.23, 86.02) * mm, "end": v(-38.6, 100.93) * mm});
            skLineSegment(sketch, "E508", {"start": v(-40.13, 86.01) * mm, "end": v(-40.23, 86.02) * mm});
            skLineSegment(sketch, "E509.0", {"start": v(32.19, 98.75) * mm, "end": v(21.95, 99.11) * mm});
            skLineSegment(sketch, "E510", {"start": v(-26.5, 100.5) * mm, "end": v(-26.5, 100.8) * mm});
            skLineSegment(sketch, "E511", {"start": v(-11.52, 99.98) * mm, "end": v(-11.5, 100.28) * mm});
            skLineSegment(sketch, "E512", {"start": v(-38.6, 100.93) * mm, "end": v(-38.57, 101.23) * mm});
            skLineSegment(sketch, "E513.trimOffspring", {"start": v(-26.5, 100.8) * mm, "end": v(-38.57, 101.23) * mm});
            skLineSegment(sketch, "E514", {"start": v(6.95, 99.33) * mm, "end": v(6.96, 99.63) * mm});
            skLineSegment(sketch, "E515", {"start": v(21.94, 98.81) * mm, "end": v(21.95, 99.11) * mm});
            skLineSegment(sketch, "E516.trimOffspring", {"start": v(6.96, 99.63) * mm, "end": v(-11.5, 100.28) * mm});
            skLineSegment(sketch, "E517", {"start": v(-64.4, 101.83) * mm, "end": v(-39.7, 100.97) * mm, "construction": true});
            skLineSegment(sketch, "E518.0", {"start": v(34.82, 83.74) * mm, "end": v(32.19, 98.75) * mm});
            skPoint(sketch, "E519.orphan", {"position": v(31.93, 98.46) * mm});
            skLineSegment(sketch, "E520.0", {"start": v(44.33, 29.57) * mm, "end": v(37.41, 68.96) * mm});
            skLineSegment(sketch, "E521.trimOffspring", {"start": v(37.12, 68.91) * mm, "end": v(31.93, 98.46) * mm, "construction": true});
            skLineSegment(sketch, "E522.0", {"start": v(49.74, -1.3) * mm, "end": v(46.92, 14.8) * mm});
            skLineSegment(sketch, "E523", {"start": v(49.44, -1.3) * mm, "end": v(49.74, -1.3) * mm});
            skLineSegment(sketch, "E524.0", {"start": v(-46.85, 25.33) * mm, "end": v(-41.85, 71.11) * mm});
            skLineSegment(sketch, "E525", {"start": v(-41.75, 71.1) * mm, "end": v(-41.85, 71.11) * mm});
            skLineSegment(sketch, "E526", {"start": v(-46.75, 25.32) * mm, "end": v(-46.85, 25.33) * mm});
            skPoint(sketch, "E527.end.orphan", {"position": v(-41.75, 71.1) * mm});
            skPoint(sketch, "E527.start.orphan", {"position": v(-40.13, 86.01) * mm});
            skLineSegment(sketch, "E528.0", {"start": v(-49.75, -1.3) * mm, "end": v(-48.47, 10.42) * mm});
            skLineSegment(sketch, "E529", {"start": v(-48.37, 10.4) * mm, "end": v(-48.47, 10.42) * mm});
            skLineSegment(sketch, "E530", {"start": v(-49.65, -1.3) * mm, "end": v(-49.75, -1.3) * mm});
            skLineSegment(sketch, "E531.trimOffspring", {"start": v(-49.65, -1.3) * mm, "end": v(-50, -4.5) * mm, "construction": true});
            skLineSegment(sketch, "E532", {"start": v(-40.13, 86.01) * mm, "end": v(-36.95, 85.66) * mm});
            skLineSegment(sketch, "E533", {"start": v(-41.75, 71.1) * mm, "end": v(-38.57, 70.75) * mm});
            skLineSegment(sketch, "E534", {"start": v(-48.37, 10.4) * mm, "end": v(-45.2, 10.06) * mm});
            skLineSegment(sketch, "E535", {"start": v(-43.57, 24.97) * mm, "end": v(-46.75, 25.32) * mm});
            skLineSegment(sketch, "E536", {"start": v(-43.57, 24.97) * mm, "end": v(-45.2, 10.06) * mm});
            skLineSegment(sketch, "E537", {"start": v(-36.95, 85.66) * mm, "end": v(-38.57, 70.75) * mm});
            skLineSegment(sketch, "E538", {"start": v(34.52, 83.69) * mm, "end": v(31.37, 83.13) * mm});
            skLineSegment(sketch, "E539", {"start": v(34.52, 83.69) * mm, "end": v(34.82, 83.74) * mm});
            skLineSegment(sketch, "E540", {"start": v(37.12, 68.91) * mm, "end": v(33.96, 68.36) * mm});
            skLineSegment(sketch, "E541", {"start": v(37.12, 68.91) * mm, "end": v(37.41, 68.96) * mm});
            skLineSegment(sketch, "E542", {"start": v(46.62, 14.74) * mm, "end": v(43.47, 14.19) * mm});
            skLineSegment(sketch, "E543", {"start": v(46.62, 14.74) * mm, "end": v(46.92, 14.8) * mm});
            skLineSegment(sketch, "E544", {"start": v(40.88, 28.96) * mm, "end": v(44.03, 29.51) * mm});
            skLineSegment(sketch, "E545", {"start": v(44.03, 29.51) * mm, "end": v(44.33, 29.57) * mm});
            skLineSegment(sketch, "E546", {"start": v(40.88, 28.96) * mm, "end": v(43.47, 14.19) * mm});
            skLineSegment(sketch, "E547", {"start": v(31.37, 83.13) * mm, "end": v(33.96, 68.36) * mm});
            skLineSegment(sketch, "E548", {"start": v(31.93, 98.46) * mm, "end": v(-38.5, 100.92) * mm, "construction": true});
            skSolve(sketch);
        }
        {
            var Q0;
            Q0 = qSketchRegion(id + "F22", true);
            extrude(context, id + "F23", {"entities" : qUnion([Q0]), "oppositeDirection" : true, "depth" : 3.2 * mm});
        }
        {
            var Q0;
            Q0=makeQuery(id+"F10.boolean.opBoolean","COPY",FACE,{"derivedFrom":makeQuery(id+"F10.opLoft","CAP_FACE",FACE,{"disambiguationData":[OSD([makeQuery(id+"F9.imprint","IMPRINT",FACE,{"disambiguationData":[TD([[makeQuery(id+"F9.imprint","IMPRINT",EDGE,{"derivedFrom":sQuery(id+"F9.wireOp",EDGE,"E4")}),1.0]])]})])],"isStart":true})});
            var sketch = newSketch(context, id + "F24", { "sketchPlane" : qUnion([Q0])});
            skLineSegment(sketch, "E549.0", {"start": v(15.07, 41.88) * mm, "end": v(-3.4, 41.91) * mm});
            skLineSegment(sketch, "E550.0", {"start": v(-3.4, 45.26) * mm, "end": v(-3.4, 41.91) * mm});
            skLineSegment(sketch, "E551.0", {"start": v(42.33, 41.84) * mm, "end": v(30.07, 41.86) * mm});
            skLineSegment(sketch, "E552.0", {"start": v(30.08, 45.2) * mm, "end": v(30.07, 41.86) * mm});
            skLineSegment(sketch, "E553.0", {"start": v(-25.66, -23.63) * mm, "end": v(-17.31, -23.62) * mm});
            skLineSegment(sketch, "E554.0", {"start": v(-17.31, -23.62) * mm, "end": v(-17.3, -26.96) * mm});
            skLineSegment(sketch, "E555.0", {"start": v(-2.31, -23.6) * mm, "end": v(-2.3, -26.93) * mm});
            skLineSegment(sketch, "E556.0", {"start": v(-17.3, -26.96) * mm, "end": v(-2.3, -26.93) * mm});
            skLineSegment(sketch, "E557.0", {"start": v(-2.31, -23.6) * mm, "end": v(15.41, -23.57) * mm});
            skLineSegment(sketch, "E558.0", {"start": v(15.41, -23.57) * mm, "end": v(15.42, -26.9) * mm});
            skLineSegment(sketch, "E559.0", {"start": v(15.42, -26.9) * mm, "end": v(30.42, -26.88) * mm});
            skLineSegment(sketch, "E560.0", {"start": v(30.41, -23.55) * mm, "end": v(30.42, -26.88) * mm});
            skLineSegment(sketch, "E561.0", {"start": v(30.41, -23.55) * mm, "end": v(39.2, -23.53) * mm});
            skLineSegment(sketch, "E562.0", {"start": v(39.2, -23.53) * mm, "end": v(39.11, -6.12) * mm});
            skLineSegment(sketch, "E563.0", {"start": v(38.98, 28.22) * mm, "end": v(38.98, 28.22) * mm});
            skLineSegment(sketch, "E564", {"start": v(7, 8.84) * mm, "end": v(7, 69.6) * mm, "construction": true});
            skLineSegment(sketch, "E565", {"start": v(7, 8.84) * mm, "end": v(51.45, 53.3) * mm, "construction": true});
            skLineSegment(sketch, "E566", {"start": v(7, 8.84) * mm, "end": v(41.55, -25.72) * mm, "construction": true});
            skLineSegment(sketch, "E567", {"start": v(7, 8.84) * mm, "end": v(-29.63, -27.8) * mm, "construction": true});
            skLineSegment(sketch, "E568", {"start": v(7, 8.84) * mm, "end": v(-29.26, 45.1) * mm, "construction": true});
            skCircle(sketch, "E569", {"center": v(7, 8.84) * mm, "radius": 10 * mm});
            skCircle(sketch, "E570", {"center": v(7, 8.84) * mm, "radius": 30 * mm, "construction": true});
            skArc(sketch, "E571", {"start": v(-12.8, 31.46) * mm, "mid": v(-15.63, 31.46) * mm, "end": v(-15.63, 28.64) * mm});
            skArc(sketch, "E572", {"start": v(29.57, 28.59) * mm, "mid": v(29.65, 31.44) * mm, "end": v(26.8, 31.46) * mm});
            skArc(sketch, "E573", {"start": v(-15.63, -10.96) * mm, "mid": v(-15.63, -13.8) * mm, "end": v(-12.8, -13.8) * mm});
            skArc(sketch, "E574", {"start": v(26.75, -13.74) * mm, "mid": v(29.6, -13.81) * mm, "end": v(29.62, -10.96) * mm});
            skCircle(sketch, "E575", {"center": v(7, 8.84) * mm, "radius": 20 * mm, "construction": true});
            skArc(sketch, "E576", {"start": v(-8.56, 21.56) * mm, "mid": v(-5.73, 21.56) * mm, "end": v(-5.73, 24.4) * mm});
            skArc(sketch, "E577", {"start": v(19.72, 24.4) * mm, "mid": v(19.72, 21.56) * mm, "end": v(22.55, 21.56) * mm});
            skArc(sketch, "E578", {"start": v(22.55, -3.9) * mm, "mid": v(19.72, -3.9) * mm, "end": v(19.72, -6.72) * mm});
            skArc(sketch, "E579", {"start": v(-5.73, -6.72) * mm, "mid": v(-5.73, -3.9) * mm, "end": v(-8.56, -3.9) * mm});
            skLineSegment(sketch, "E580.trimOffspring", {"start": v(22.55, 21.56) * mm, "end": v(29.62, 28.64) * mm});
            skLineSegment(sketch, "E581.trimOffspring", {"start": v(19.72, 24.4) * mm, "end": v(26.8, 31.46) * mm});
            skLineSegment(sketch, "E582.trimOffspring", {"start": v(-8.56, 21.56) * mm, "end": v(-15.63, 28.64) * mm});
            skLineSegment(sketch, "E583.trimOffspring", {"start": v(-5.73, 24.4) * mm, "end": v(-12.8, 31.46) * mm});
            skLineSegment(sketch, "E584.trimOffspring", {"start": v(-5.73, -6.72) * mm, "end": v(-12.8, -13.8) * mm});
            skLineSegment(sketch, "E585.trimOffspring", {"start": v(-8.56, -3.9) * mm, "end": v(-15.63, -10.96) * mm});
            skLineSegment(sketch, "E586.trimOffspring", {"start": v(19.72, -6.72) * mm, "end": v(26.75, -13.74) * mm});
            skLineSegment(sketch, "E587.trimOffspring", {"start": v(22.55, -3.9) * mm, "end": v(29.62, -10.96) * mm});
            skLineSegment(sketch, "E588.0", {"start": v(-5.41, 34.18) * mm, "end": v(19.19, 34.14) * mm});
            skArc(sketch, "E589.0", {"start": v(-5.41, 34.18) * mm, "mid": v(-6.34, 33.56) * mm, "end": v(-6.12, 32.47) * mm});
            skLineSegment(sketch, "E590.0", {"start": v(-6.12, 32.47) * mm, "end": v(-6.12, 32.47) * mm});
            skLineSegment(sketch, "E591.0", {"start": v(-16.96, 22.1) * mm, "end": v(-16.96, 22.1) * mm});
            skArc(sketch, "E592.0", {"start": v(-18.87, -4.09) * mm, "mid": v(-18.25, -5.02) * mm, "end": v(-17.16, -4.8) * mm});
            skLineSegment(sketch, "E593.0", {"start": v(-18.67, 21.4) * mm, "end": v(-18.87, -4.09) * mm});
            skArc(sketch, "E594.0", {"start": v(-16.96, 22.1) * mm, "mid": v(-18.05, 22.32) * mm, "end": v(-18.67, 21.4) * mm});
            skLineSegment(sketch, "E595.0", {"start": v(18.7, -15.8) * mm, "end": v(18.7, -15.8) * mm});
            skArc(sketch, "E596.0", {"start": v(-5.28, -14.13) * mm, "mid": v(-5.5, -15.22) * mm, "end": v(-4.57, -15.84) * mm});
            skLineSegment(sketch, "E597.0", {"start": v(-4.57, -15.84) * mm, "end": v(18.7, -15.8) * mm});
            skLineSegment(sketch, "E598.0", {"start": v(32.42, 21.33) * mm, "end": v(32.42, 21.33) * mm});
            skLineSegment(sketch, "E599.0", {"start": v(32.54, -3.6) * mm, "end": v(32.54, -3.6) * mm});
            skLineSegment(sketch, "E600.0", {"start": v(32.42, 21.33) * mm, "end": v(32.54, -3.6) * mm});
            skLineSegment(sketch, "E601.0", {"start": v(-16.96, 22.1) * mm, "end": v(-10.34, 15.5) * mm});
            skArc(sketch, "E602.0", {"start": v(-10.1, 14.48) * mm, "mid": v(-10.07, 15.03) * mm, "end": v(-10.34, 15.5) * mm});
            skArc(sketch, "E603.0", {"start": v(-10.1, 14.48) * mm, "mid": v(-11, 8.8) * mm, "end": v(-10.07, 3.1) * mm});
            skArc(sketch, "E604.0", {"start": v(-10.3, 2.08) * mm, "mid": v(-10.04, 2.56) * mm, "end": v(-10.07, 3.1) * mm});
            skLineSegment(sketch, "E605.0", {"start": v(-17.16, -4.8) * mm, "end": v(-10.3, 2.08) * mm});
            skArc(sketch, "E606.0", {"start": v(19.9, 32.43) * mm, "mid": v(20.11, 33.52) * mm, "end": v(19.19, 34.14) * mm});
            skLineSegment(sketch, "E607.0", {"start": v(13.67, 26.17) * mm, "end": v(19.9, 32.43) * mm});
            skArc(sketch, "E608.0", {"start": v(12.64, 25.93) * mm, "mid": v(13.19, 25.9) * mm, "end": v(13.67, 26.17) * mm});
            skArc(sketch, "E609.0", {"start": v(0.24, 26.14) * mm, "mid": v(0.72, 25.87) * mm, "end": v(1.26, 25.9) * mm});
            skArc(sketch, "E610.0", {"start": v(12.64, 25.93) * mm, "mid": v(6.95, 26.84) * mm, "end": v(1.26, 25.9) * mm});
            skLineSegment(sketch, "E611.0", {"start": v(-6.12, 32.47) * mm, "end": v(0.24, 26.14) * mm});
            skArc(sketch, "E612.0", {"start": v(32.42, 21.33) * mm, "mid": v(31.8, 22.25) * mm, "end": v(30.7, 22.03) * mm});
            skLineSegment(sketch, "E613.0", {"start": v(24.3, 15.6) * mm, "end": v(30.7, 22.03) * mm});
            skArc(sketch, "E614.0", {"start": v(24.3, 15.6) * mm, "mid": v(24.03, 15.11) * mm, "end": v(24.06, 14.57) * mm});
            skArc(sketch, "E615.0", {"start": v(24.09, 3.19) * mm, "mid": v(24.06, 2.64) * mm, "end": v(24.33, 2.17) * mm});
            skArc(sketch, "E616.0", {"start": v(30.83, -4.3) * mm, "mid": v(31.92, -4.52) * mm, "end": v(32.54, -3.6) * mm});
            skLineSegment(sketch, "E617.0", {"start": v(24.33, 2.17) * mm, "end": v(30.83, -4.3) * mm});
            skArc(sketch, "E618.0", {"start": v(24.09, 3.19) * mm, "mid": v(25, 8.88) * mm, "end": v(24.06, 14.57) * mm});
            skArc(sketch, "E619.0", {"start": v(18.7, -15.8) * mm, "mid": v(19.62, -15.18) * mm, "end": v(19.4, -14.1) * mm});
            skArc(sketch, "E620.0", {"start": v(1.35, -8.25) * mm, "mid": v(0.8, -8.23) * mm, "end": v(0.32, -8.5) * mm});
            skArc(sketch, "E621.0", {"start": v(13.75, -8.47) * mm, "mid": v(13.27, -8.2) * mm, "end": v(12.73, -8.23) * mm});
            skArc(sketch, "E622.0", {"start": v(1.35, -8.25) * mm, "mid": v(7.04, -9.16) * mm, "end": v(12.73, -8.23) * mm});
            skLineSegment(sketch, "E623.0", {"start": v(13.75, -8.47) * mm, "end": v(19.4, -14.1) * mm});
            skLineSegment(sketch, "E624.0", {"start": v(-5.28, -14.13) * mm, "end": v(0.32, -8.5) * mm});
            skLineSegment(sketch, "E625.0", {"start": v(-29.65, 41.95) * mm, "end": v(-29.72, 33.17) * mm});
            skLineSegment(sketch, "E626.0", {"start": v(-29.84, 18.17) * mm, "end": v(-30.02, -5.51) * mm});
            skLineSegment(sketch, "E627.0", {"start": v(-3.4, 45.26) * mm, "end": v(-18.4, 45.29) * mm});
            skLineSegment(sketch, "E628.0", {"start": v(30.08, 45.2) * mm, "end": v(15.08, 45.23) * mm});
            skLineSegment(sketch, "E629", {"start": v(-18.4, 45.14) * mm, "end": v(-18.4, 45.29) * mm});
            skLineSegment(sketch, "E630", {"start": v(15.08, 45.09) * mm, "end": v(15.08, 45.23) * mm});
            skLineSegment(sketch, "E631", {"start": v(30.08, 45.2) * mm, "end": v(30.08, 45.2) * mm});
            skLineSegment(sketch, "E632.0", {"start": v(42.38, 30.04) * mm, "end": v(42.33, 41.84) * mm});
            skLineSegment(sketch, "E633.0", {"start": v(42.56, -6.1) * mm, "end": v(42.46, 15.04) * mm});
            skLineSegment(sketch, "E634", {"start": v(42.38, 30.04) * mm, "end": v(42.38, 30.04) * mm});
            skLineSegment(sketch, "E635", {"start": v(42.33, 41.84) * mm, "end": v(42.33, 41.84) * mm});
            skPoint(sketch, "E636.orphan", {"position": v(42.33, 41.99) * mm});
            skLineSegment(sketch, "E637", {"start": v(42.22, 15.04) * mm, "end": v(42.46, 15.04) * mm});
            skLineSegment(sketch, "E638", {"start": v(42.56, -6.1) * mm, "end": v(42.56, -6.1) * mm});
            skLineSegment(sketch, "E639", {"start": v(-18.4, 45.14) * mm, "end": v(-18.4, 41.94) * mm});
            skLineSegment(sketch, "E640", {"start": v(15.08, 45.09) * mm, "end": v(15.07, 41.88) * mm});
            skLineSegment(sketch, "E641", {"start": v(42.22, 15.04) * mm, "end": v(39, 15.03) * mm});
            skLineSegment(sketch, "E642", {"start": v(-28.4, 45.16) * mm, "end": v(-28.96, -27.3) * mm, "construction": true});
            skLineSegment(sketch, "E643", {"start": v(-28.5, 33.16) * mm, "end": v(-25.22, 33.13) * mm});
            skLineSegment(sketch, "E644", {"start": v(-28.5, 33.16) * mm, "end": v(-29.72, 33.17) * mm});
            skLineSegment(sketch, "E645", {"start": v(-28.6, 18.16) * mm, "end": v(-25.34, 18.13) * mm});
            skLineSegment(sketch, "E646", {"start": v(-28.6, 18.16) * mm, "end": v(-29.84, 18.17) * mm});
            skLineSegment(sketch, "E647", {"start": v(-25.34, 18.13) * mm, "end": v(-25.22, 33.13) * mm});
            skLineSegment(sketch, "E648", {"start": v(-28.8, -5.52) * mm, "end": v(-25.52, -5.55) * mm});
            skLineSegment(sketch, "E649", {"start": v(-28.8, -5.52) * mm, "end": v(-30.02, -5.51) * mm});
            skLineSegment(sketch, "E650", {"start": v(-25.52, -5.55) * mm, "end": v(-25.66, -23.63) * mm});
            skLineSegment(sketch, "E651", {"start": v(-18.4, 41.94) * mm, "end": v(-29.65, 41.95) * mm});
            skPoint(sketch, "E652.0", {"position": v(42.08, 45.04) * mm});
            skLineSegment(sketch, "E653", {"start": v(42.15, 30.04) * mm, "end": v(38.94, 30.03) * mm});
            skLineSegment(sketch, "E654", {"start": v(42.15, 30.04) * mm, "end": v(42.38, 30.04) * mm});
            skLineSegment(sketch, "E655", {"start": v(39, 15.03) * mm, "end": v(38.94, 30.03) * mm});
            skLineSegment(sketch, "E656", {"start": v(42.32, -6.1) * mm, "end": v(39.11, -6.12) * mm});
            skLineSegment(sketch, "E657", {"start": v(42.32, -6.1) * mm, "end": v(42.56, -6.1) * mm});
            skCircle(sketch, "E658", {"center": v(7, 38.84) * mm, "radius": 1 * mm});
            skSolve(sketch);
        }
        {
            var Q0;
            Q0 = qSketchRegion(id + "F24", true);
            extrude(context, id + "F25", {"entities" : qUnion([Q0]), "oppositeDirection" : true, "depth" : 3.2 * mm});
        }
        {
            var Q0;
            Q0=makeQuery(id+"F15.opExtrude","CAP_FACE",FACE,{"disambiguationData":[OSD([sQuery(id+"F14.wireOp",EDGE,"629dc714-f1a2-4748-8174-6bdeec1f6e5700"),sQuery(id+"F14.wireOp",EDGE,"90850073-97a5-4d5f-8fec-853776653e4100"),sQuery(id+"F14.wireOp",EDGE,"2b481087-0edc-4ba4-bb79-bd8afdd554dd00"),sQuery(id+"F14.wireOp",EDGE,"E89"),sQuery(id+"F14.wireOp",EDGE,"E92.0"),sQuery(id+"F14.wireOp",EDGE,"E92.1"),sQuery(id+"F14.wireOp",EDGE,"E92.2"),sQuery(id+"F14.wireOp",EDGE,"E92.3"),sQuery(id+"F14.wireOp",EDGE,"IerrKZlL-V5Zz-XRSl-Df7s-29j93G1HJUvt"),sQuery(id+"F14.wireOp",EDGE,"E93"),sQuery(id+"F14.wireOp",EDGE,"E94"),sQuery(id+"F14.wireOp",EDGE,"E95"),sQuery(id+"F14.wireOp",EDGE,"E96"),sQuery(id+"F14.wireOp",EDGE,"E97"),sQuery(id+"F14.wireOp",EDGE,"E98"),sQuery(id+"F14.wireOp",EDGE,"E99"),sQuery(id+"F14.wireOp",EDGE,"E100.trimOffspring"),sQuery(id+"F14.wireOp",EDGE,"E101.trimOffspring"),sQuery(id+"F14.wireOp",EDGE,"E102.trimOffspring"),sQuery(id+"F14.wireOp",EDGE,"E103.trimOffspring"),sQuery(id+"F14.wireOp",EDGE,"E107.0"),sQuery(id+"F14.wireOp",EDGE,"E108.0"),sQuery(id+"F14.wireOp",EDGE,"E109.0"),sQuery(id+"F14.wireOp",EDGE,"E110.0"),sQuery(id+"F14.wireOp",EDGE,"E111.0"),sQuery(id+"F14.wireOp",EDGE,"E112.0"),sQuery(id+"F14.wireOp",EDGE,"E113.0"),sQuery(id+"F14.wireOp",EDGE,"E114.0"),sQuery(id+"F14.wireOp",EDGE,"E115.0"),sQuery(id+"F14.wireOp",EDGE,"E116.0"),sQuery(id+"F14.wireOp",EDGE,"E117.0"),sQuery(id+"F14.wireOp",EDGE,"E118.0"),sQuery(id+"F14.wireOp",EDGE,"E119.0"),sQuery(id+"F14.wireOp",EDGE,"E120.0"),sQuery(id+"F14.wireOp",EDGE,"E121.0"),sQuery(id+"F14.wireOp",EDGE,"E122.0"),sQuery(id+"F14.wireOp",EDGE,"E123.0")])],"isStart":true});
            var sketch = newSketch(context, id + "F26", { "sketchPlane" : qUnion([Q0])});
            skLineSegment(sketch, "E659.0", {"start": v(19.26, 24.85) * mm, "end": v(26.31, 31.94) * mm});
            skArc(sketch, "E660.0", {"start": v(30, 28.27) * mm, "mid": v(30, 31.94) * mm, "end": v(26.31, 31.94) * mm});
            skLineSegment(sketch, "E661.0", {"start": v(22.95, 21.18) * mm, "end": v(30, 28.27) * mm});
            skArc(sketch, "E662.0", {"start": v(19.26, 24.85) * mm, "mid": v(19.27, 21.17) * mm, "end": v(22.95, 21.18) * mm});
            skCircle(sketch, "E663.0", {"center": v(7, 8.84) * mm, "radius": 10 * mm});
            skArc(sketch, "E664.0", {"start": v(-12.43, 31.84) * mm, "mid": v(-16.11, 31.83) * mm, "end": v(-16.1, 28.16) * mm});
            skLineSegment(sketch, "E665.0", {"start": v(-5.35, 24.79) * mm, "end": v(-12.43, 31.84) * mm});
            skLineSegment(sketch, "E666.0", {"start": v(-9.02, 21.1) * mm, "end": v(-16.1, 28.16) * mm});
            skArc(sketch, "E667.0", {"start": v(-9.02, 21.1) * mm, "mid": v(-5.34, 21.11) * mm, "end": v(-5.35, 24.79) * mm});
            skArc(sketch, "E668.0", {"start": v(-5.27, -7.17) * mm, "mid": v(-5.28, -3.5) * mm, "end": v(-8.96, -3.5) * mm});
            skLineSegment(sketch, "E669.0", {"start": v(-5.27, -7.17) * mm, "end": v(-12.32, -14.26) * mm});
            skLineSegment(sketch, "E670.0", {"start": v(-8.96, -3.5) * mm, "end": v(-16, -10.6) * mm});
            skArc(sketch, "E671.0", {"start": v(-16, -10.6) * mm, "mid": v(-16, -14.27) * mm, "end": v(-12.32, -14.26) * mm});
            skArc(sketch, "E672.0", {"start": v(23, -3.43) * mm, "mid": v(19.33, -3.44) * mm, "end": v(19.34, -7.11) * mm});
            skLineSegment(sketch, "E673.0", {"start": v(23, -3.43) * mm, "end": v(30.1, -10.48) * mm});
            skLineSegment(sketch, "E674.0", {"start": v(19.34, -7.11) * mm, "end": v(26.43, -14.17) * mm});
            skArc(sketch, "E675.0", {"start": v(26.43, -14.17) * mm, "mid": v(30.1, -14.16) * mm, "end": v(30.1, -10.48) * mm});
            skArc(sketch, "E676", {"start": v(33.47, 24.81) * mm, "mid": v(33.45, 35.42) * mm, "end": v(22.84, 35.4) * mm});
            skArc(sketch, "E677", {"start": v(22.97, -17.64) * mm, "mid": v(33.58, -17.62) * mm, "end": v(33.55, -7) * mm});
            skArc(sketch, "E678.trimOffspring", {"start": v(-8.98, 35.32) * mm, "mid": v(-19.59, 35.29) * mm, "end": v(-19.56, 24.68) * mm});
            skArc(sketch, "E679.trimOffspring", {"start": v(-19.48, -7.14) * mm, "mid": v(-19.46, -17.74) * mm, "end": v(-8.85, -17.72) * mm});
            skLineSegment(sketch, "E680", {"start": v(-8.98, 35.32) * mm, "end": v(0.24, 26.14) * mm});
            skLineSegment(sketch, "E681", {"start": v(-19.56, 24.68) * mm, "end": v(-10.34, 15.5) * mm});
            skLineSegment(sketch, "E682", {"start": v(-8.85, -17.72) * mm, "end": v(0.32, -8.5) * mm});
            skLineSegment(sketch, "E683", {"start": v(22.84, 35.4) * mm, "end": v(13.67, 26.17) * mm});
            skLineSegment(sketch, "E684.trimOffspring", {"start": v(-10.3, 2.08) * mm, "end": v(-19.48, -7.14) * mm});
            skArc(sketch, "E685.trimOffspring", {"start": v(-10.1, 14.48) * mm, "mid": v(-11, 8.8) * mm, "end": v(-10.07, 3.1) * mm});
            skArc(sketch, "E686.trimOffspring", {"start": v(1.35, -8.25) * mm, "mid": v(7.04, -9.16) * mm, "end": v(12.73, -8.23) * mm});
            skLineSegment(sketch, "E687.trimOffspring", {"start": v(13.75, -8.47) * mm, "end": v(22.97, -17.64) * mm});
            skLineSegment(sketch, "E688.trimOffspring", {"start": v(24.33, 2.17) * mm, "end": v(33.55, -7) * mm});
            skArc(sketch, "E689.trimOffspring", {"start": v(24.09, 3.19) * mm, "mid": v(25, 8.88) * mm, "end": v(24.06, 14.57) * mm});
            skLineSegment(sketch, "E690.trimOffspring", {"start": v(24.3, 15.6) * mm, "end": v(33.47, 24.81) * mm});
            skArc(sketch, "E691.trimOffspring", {"start": v(12.64, 25.93) * mm, "mid": v(6.95, 26.84) * mm, "end": v(1.26, 25.9) * mm});
            skLineSegment(sketch, "E692", {"start": v(-14.27, 30) * mm, "end": v(28.26, -12.33) * mm, "construction": true});
            skLineSegment(sketch, "E693", {"start": v(28.16, 30.1) * mm, "end": v(-14.17, -12.43) * mm, "construction": true});
            skPoint(sketch, "E694.visualSharp", {"position": v(-9.9, 15.06) * mm});
            skArc(sketch, "E694.filletArc", {"start": v(-10.1, 14.48) * mm, "mid": v(-10.07, 15.03) * mm, "end": v(-10.34, 15.5) * mm});
            skPoint(sketch, "E695.visualSharp", {"position": v(-9.86, 2.53) * mm});
            skArc(sketch, "E695.filletArc", {"start": v(-10.3, 2.08) * mm, "mid": v(-10.04, 2.56) * mm, "end": v(-10.07, 3.1) * mm});
            skPoint(sketch, "E696.visualSharp", {"position": v(0.77, -8.05) * mm});
            skArc(sketch, "E696.filletArc", {"start": v(1.35, -8.25) * mm, "mid": v(0.8, -8.23) * mm, "end": v(0.32, -8.5) * mm});
            skPoint(sketch, "E697.visualSharp", {"position": v(13.3, -8.02) * mm});
            skArc(sketch, "E697.filletArc", {"start": v(13.75, -8.47) * mm, "mid": v(13.27, -8.2) * mm, "end": v(12.73, -8.23) * mm});
            skPoint(sketch, "E698.visualSharp", {"position": v(23.88, 2.61) * mm});
            skArc(sketch, "E698.filletArc", {"start": v(24.09, 3.19) * mm, "mid": v(24.06, 2.64) * mm, "end": v(24.33, 2.17) * mm});
            skPoint(sketch, "E699.visualSharp", {"position": v(23.85, 15.14) * mm});
            skArc(sketch, "E699.filletArc", {"start": v(24.3, 15.6) * mm, "mid": v(24.03, 15.11) * mm, "end": v(24.06, 14.57) * mm});
            skPoint(sketch, "E700.visualSharp", {"position": v(13.22, 25.73) * mm});
            skArc(sketch, "E700.filletArc", {"start": v(12.64, 25.93) * mm, "mid": v(13.19, 25.9) * mm, "end": v(13.67, 26.17) * mm});
            skPoint(sketch, "E701.visualSharp", {"position": v(0.69, 25.7) * mm});
            skArc(sketch, "E701.filletArc", {"start": v(0.24, 26.14) * mm, "mid": v(0.72, 25.87) * mm, "end": v(1.26, 25.9) * mm});
            skSolve(sketch);
        }
        {
            var Q0;
            Q0 = qSketchRegion(id + "F26", true);
            extrude(context, id + "F27", {"entities" : qUnion([Q0]), "depth" : 3 * mm});
        }
        {
            var Q0;
            Q0=makeQuery(id+"F12.opExtrude","SWEPT_FACE",FACE,{"disambiguationData":[OSD([sQuery(id+"F11.wireOp",EDGE,"E54.trimOffspring")])]});
            cPlane(context, id + "F28", {"entities" : qUnion([Q0]), "cplaneType" : CPlaneType.OFFSET, "offset" : 0 * mm, "oppositeDirection" : true, "width" : 150 * mm, "height" : 150 * mm});
        }
        {
            var Q0;
            Q0=qCreatedBy(id+"F28.planeOp",FACE);
            var sketch = newSketch(context, id + "F29", { "sketchPlane" : qUnion([Q0])});
            skLineSegment(sketch, "E702", {"start": v(-31.2, 3.2) * mm, "end": v(-36.2, 3.2) * mm});
            skLineSegment(sketch, "E703", {"start": v(-36.2, 3.2) * mm, "end": v(-56.2, 3.2) * mm});
            skLineSegment(sketch, "E704", {"start": v(-71.2, 3.2) * mm, "end": v(-76.6, 3.2) * mm});
            skLineSegment(sketch, "E705", {"start": v(-31.2, 48.2) * mm, "end": v(-31.2, 75) * mm});
            skLineSegment(sketch, "E706", {"start": v(-31.2, 3.2) * mm, "end": v(-31.2, 33.2) * mm});
            skLineSegment(sketch, "E707", {"start": v(-71.2, 0) * mm, "end": v(-56.2, 0) * mm});
            skLineSegment(sketch, "E708", {"start": v(-71.2, 3.2) * mm, "end": v(-71.2, 0) * mm});
            skLineSegment(sketch, "E709", {"start": v(-56.2, 3.2) * mm, "end": v(-56.2, 0) * mm});
            skPoint(sketch, "E710.start.orphan", {"position": v(-36.2, 0) * mm});
            skPoint(sketch, "E711.start.orphan", {"position": v(-31.2, 0) * mm});
            skPoint(sketch, "E712.orphan", {"position": v(-28, 33.2) * mm});
            skPoint(sketch, "E713.start.orphan", {"position": v(-28, 48.2) * mm});
            skLineSegment(sketch, "E714", {"start": v(-31.2, 48.2) * mm, "end": v(-28, 48.2) * mm});
            skLineSegment(sketch, "E715", {"start": v(-31.2, 33.2) * mm, "end": v(-28, 33.2) * mm});
            skPoint(sketch, "E716.end.orphan", {"position": v(-31.2, 48.2) * mm});
            skPoint(sketch, "E717.end.orphan", {"position": v(-28, 99.35) * mm});
            skLineSegment(sketch, "E718", {"start": v(-86.2, 3.2) * mm, "end": v(-76.6, 3.2) * mm});
            skLineSegment(sketch, "E719", {"start": v(-31.2, 75) * mm, "end": v(-76.2, 75) * mm});
            skPoint(sketch, "E720.orphan", {"position": v(38.31, 93.65) * mm});
            skPoint(sketch, "E721.start.orphan", {"position": v(-31.2, 99.35) * mm});
            skPoint(sketch, "E722.visualSharp", {"position": v(-86.2, 75) * mm});
            skLineSegment(sketch, "E723.0", {"start": v(-83, 9) * mm, "end": v(-83, 21) * mm});
            skLineSegment(sketch, "E724", {"start": v(-86.2, 63) * mm, "end": v(-83, 63) * mm});
            skLineSegment(sketch, "E725", {"start": v(-86.2, 51) * mm, "end": v(-83, 51) * mm});
            skLineSegment(sketch, "E726", {"start": v(-86.2, 21) * mm, "end": v(-83, 21) * mm});
            skLineSegment(sketch, "E727", {"start": v(-86.2, 9) * mm, "end": v(-83, 9) * mm});
            skLineSegment(sketch, "E728", {"start": v(-31.2, 75) * mm, "end": v(-86.2, 3.2) * mm, "construction": true});
            skLineSegment(sketch, "E729", {"start": v(-86.2, 75) * mm, "end": v(-31.2, 3.2) * mm, "construction": true});
            skLineSegment(sketch, "E730", {"start": v(-73, 67) * mm, "end": v(-44.4, 67) * mm});
            skLineSegment(sketch, "E731", {"start": v(-76, 52.16) * mm, "end": v(-76, 26.04) * mm});
            skLineSegment(sketch, "E732", {"start": v(-73.77, 10.2) * mm, "end": v(-43.63, 10.2) * mm});
            skLineSegment(sketch, "E733", {"start": v(-38.2, 56.33) * mm, "end": v(-38.2, 21.87) * mm});
            skLineSegment(sketch, "E734.trimOffspring", {"start": v(-74.2, 52.76) * mm, "end": v(-64.2, 39.7) * mm});
            skLineSegment(sketch, "E735.trimOffspring", {"start": v(-73.8, 65.4) * mm, "end": v(-59.5, 46.71) * mm});
            skLineSegment(sketch, "E736.trimOffspring", {"start": v(-43.6, 65.4) * mm, "end": v(-57.9, 46.71) * mm});
            skLineSegment(sketch, "E737.trimOffspring", {"start": v(-40, 56.94) * mm, "end": v(-53.2, 39.7) * mm});
            skLineSegment(sketch, "E738.trimOffspring", {"start": v(-57.9, 31.49) * mm, "end": v(-42.83, 11.8) * mm});
            skLineSegment(sketch, "E739.trimOffspring", {"start": v(-64.2, 38.5) * mm, "end": v(-74.2, 25.44) * mm});
            skLineSegment(sketch, "E740.trimOffspring", {"start": v(-59.5, 31.49) * mm, "end": v(-74.57, 11.8) * mm});
            skLineSegment(sketch, "E741.trimOffspring", {"start": v(-53.2, 38.5) * mm, "end": v(-40, 21.26) * mm});
            skPoint(sketch, "E742.visualSharp", {"position": v(-76, 23.1) * mm});
            skArc(sketch, "E742.filletArc", {"start": v(-76, 26.04) * mm, "mid": v(-75.32, 25.1) * mm, "end": v(-74.2, 25.44) * mm});
            skPoint(sketch, "E743.visualSharp", {"position": v(-75.8, 10.2) * mm});
            skArc(sketch, "E743.filletArc", {"start": v(-74.57, 11.8) * mm, "mid": v(-74.67, 10.76) * mm, "end": v(-73.77, 10.2) * mm});
            skPoint(sketch, "E744.visualSharp", {"position": v(-58.7, 32.52) * mm});
            skArc(sketch, "E744.filletArc", {"start": v(-57.9, 31.49) * mm, "mid": v(-58.7, 31.88) * mm, "end": v(-59.5, 31.49) * mm});
            skPoint(sketch, "E745.visualSharp", {"position": v(-41.6, 10.2) * mm});
            skArc(sketch, "E745.filletArc", {"start": v(-43.63, 10.2) * mm, "mid": v(-42.73, 10.76) * mm, "end": v(-42.83, 11.8) * mm});
            skPoint(sketch, "E746.visualSharp", {"position": v(-38.2, 18.92) * mm});
            skArc(sketch, "E746.filletArc", {"start": v(-40, 21.26) * mm, "mid": v(-38.88, 20.92) * mm, "end": v(-38.2, 21.87) * mm});
            skPoint(sketch, "E747.visualSharp", {"position": v(-38.2, 59.28) * mm});
            skArc(sketch, "E747.filletArc", {"start": v(-38.2, 56.33) * mm, "mid": v(-38.88, 57.28) * mm, "end": v(-40, 56.94) * mm});
            skPoint(sketch, "E748.visualSharp", {"position": v(-53.66, 39.1) * mm});
            skArc(sketch, "E748.filletArc", {"start": v(-53.2, 39.7) * mm, "mid": v(-53.4, 39.1) * mm, "end": v(-53.2, 38.5) * mm});
            skPoint(sketch, "E749.visualSharp", {"position": v(-42.37, 67) * mm});
            skArc(sketch, "E749.filletArc", {"start": v(-43.6, 65.4) * mm, "mid": v(-43.5, 66.44) * mm, "end": v(-44.4, 67) * mm});
            skPoint(sketch, "E750.visualSharp", {"position": v(-58.7, 45.68) * mm});
            skArc(sketch, "E750.filletArc", {"start": v(-59.5, 46.71) * mm, "mid": v(-58.7, 46.32) * mm, "end": v(-57.9, 46.71) * mm});
            skPoint(sketch, "E751.visualSharp", {"position": v(-75.03, 67) * mm});
            skArc(sketch, "E751.filletArc", {"start": v(-73, 67) * mm, "mid": v(-73.9, 66.44) * mm, "end": v(-73.8, 65.4) * mm});
            skPoint(sketch, "E752.visualSharp", {"position": v(-63.74, 39.1) * mm});
            skArc(sketch, "E752.filletArc", {"start": v(-64.2, 38.5) * mm, "mid": v(-64, 39.1) * mm, "end": v(-64.2, 39.7) * mm});
            skPoint(sketch, "E753.visualSharp", {"position": v(-76, 55.1) * mm});
            skArc(sketch, "E753.filletArc", {"start": v(-74.2, 52.76) * mm, "mid": v(-75.32, 53.1) * mm, "end": v(-76, 52.16) * mm});
            skLineSegment(sketch, "E754.trimOffspring", {"start": v(-83, 51) * mm, "end": v(-83, 63) * mm});
            skLineSegment(sketch, "E755", {"start": v(-86.2, 51) * mm, "end": v(-86.2, 56) * mm});
            skLineSegment(sketch, "E756", {"start": v(-86.2, 56) * mm, "end": v(-86.4, 56) * mm});
            skLineSegment(sketch, "E757", {"start": v(-89.4, 53.22) * mm, "end": v(-91.2, 28.3) * mm});
            skLineSegment(sketch, "E758", {"start": v(-91.2, 28.1) * mm, "end": v(-91.2, 3.2) * mm});
            skLineSegment(sketch, "E759", {"start": v(-91.2, 3.2) * mm, "end": v(-86.2, 3.2) * mm});
            skLineSegment(sketch, "E760", {"start": v(-86.2, 9) * mm, "end": v(-86.2, 21) * mm});
            skPoint(sketch, "E761.visualSharp", {"position": v(-89.2, 56) * mm});
            skArc(sketch, "E761.filletArc", {"start": v(-86.4, 56) * mm, "mid": v(-88.45, 55.2) * mm, "end": v(-89.4, 53.22) * mm});
            skPoint(sketch, "E762.visualSharp", {"position": v(-91.2, 28.2) * mm});
            skArc(sketch, "E762.filletArc", {"start": v(-91.2, 28.3) * mm, "mid": v(-91.2, 28.2) * mm, "end": v(-91.2, 28.1) * mm});
            skPoint(sketch, "E763.0", {"position": v(-86.2, 3.2) * mm});
            skLineSegment(sketch, "E764", {"start": v(-86.2, 63) * mm, "end": v(-86.2, 65) * mm});
            skArc(sketch, "E765.filletArc", {"start": v(-76.2, 75) * mm, "mid": v(-83.27, 72.07) * mm, "end": v(-86.2, 65) * mm});
            skLineSegment(sketch, "E766.0", {"start": v(-24, 35.7) * mm, "end": v(-24, 45.7) * mm});
            skLineSegment(sketch, "E767", {"start": v(-26.5, 48.2) * mm, "end": v(-28, 48.2) * mm});
            skLineSegment(sketch, "E768", {"start": v(-26.5, 33.2) * mm, "end": v(-28, 33.2) * mm});
            skLineSegment(sketch, "E769", {"start": v(-28, 48.2) * mm, "end": v(-28, 33.2) * mm, "construction": true});
            skLineSegment(sketch, "E770.0", {"start": v(-27.5, 44.7) * mm, "end": v(-27.5, 36.7) * mm, "construction": true});
            skPoint(sketch, "E771", {"position": v(-28, 40.7) * mm});
            skPoint(sketch, "E772", {"position": v(-27.5, 40.7) * mm});
            skArc(sketch, "E773.0.startCap", {"start": v(-28.5, 44.7) * mm, "mid": v(-27.5, 45.7) * mm, "end": v(-26.5, 44.7) * mm});
            skArc(sketch, "E773.0.endCap", {"start": v(-26.5, 36.7) * mm, "mid": v(-27.5, 35.7) * mm, "end": v(-28.5, 36.7) * mm});
            skLineSegment(sketch, "E773.0.left", {"start": v(-26.5, 44.7) * mm, "end": v(-26.5, 36.7) * mm});
            skLineSegment(sketch, "E773.0.right", {"start": v(-28.5, 44.7) * mm, "end": v(-28.5, 36.7) * mm});
            skPoint(sketch, "E774.visualSharp", {"position": v(-24, 48.2) * mm});
            skArc(sketch, "E774.filletArc", {"start": v(-24, 45.7) * mm, "mid": v(-24.73, 47.47) * mm, "end": v(-26.5, 48.2) * mm});
            skPoint(sketch, "E775.visualSharp", {"position": v(-24, 33.2) * mm});
            skArc(sketch, "E775.filletArc", {"start": v(-26.5, 33.2) * mm, "mid": v(-24.73, 33.93) * mm, "end": v(-24, 35.7) * mm});
            skSolve(sketch);
        }
        {
            var Q0;
            Q0 = qSketchRegion(id + "F29", true);
            extrude(context, id + "F30", {"entities" : qUnion([Q0]), "oppositeDirection" : true, "depth" : 3.2 * mm});
        }
        {
            var Q0;
            Q0=qCreatedBy(makeId("Top.planeOp"),FACE);
            var sketch = newSketch(context, id + "F31", { "sketchPlane" : qUnion([Q0])});
            skCircle(sketch, "E776", {"center": v(0, 0) * mm, "radius": 110 * mm});
            skCircle(sketch, "E777", {"center": v(0, 0) * mm, "radius": 109.5 * mm});
            skSolve(sketch);
        }
        {
            var Q0;
            Q0=makeQuery(id+"F12.opExtrude","SWEPT_FACE",FACE,{"disambiguationData":[OSD([sQuery(id+"F11.wireOp",EDGE,"E55.trimOffspring")])]});
            cPlane(context, id + "F32", {"entities" : qUnion([Q0]), "cplaneType" : CPlaneType.OFFSET, "offset" : 0 * mm, "oppositeDirection" : true, "width" : 150 * mm, "height" : 150 * mm});
        }
        {
            var Q0;
            Q0=qCreatedBy(id+"F32.planeOp",FACE);
            var sketch = newSketch(context, id + "F33", { "sketchPlane" : qUnion([Q0])});
            skLineSegment(sketch, "E778.0.1", {"start": v(86.2, 21) * mm, "end": v(83, 21) * mm});
            skLineSegment(sketch, "E778.0.2", {"start": v(83, 21) * mm, "end": v(83, 9) * mm});
            skLineSegment(sketch, "E778.0.3", {"start": v(83, 9) * mm, "end": v(83, 9) * mm});
            skLineSegment(sketch, "E778.0.6", {"start": v(71.2, 3.2) * mm, "end": v(71.2, 0) * mm});
            skLineSegment(sketch, "E778.0.7", {"start": v(71.2, 0) * mm, "end": v(56.2, 0) * mm});
            skLineSegment(sketch, "E778.0.8", {"start": v(56.2, 0) * mm, "end": v(56.2, 3.2) * mm});
            skLineSegment(sketch, "E778.0.9", {"start": v(56.2, 3.2) * mm, "end": v(31.2, 3.2) * mm});
            skLineSegment(sketch, "E778.0.10", {"start": v(31.2, 3.2) * mm, "end": v(31.2, 33.2) * mm});
            skLineSegment(sketch, "E778.0.11", {"start": v(31.2, 33.2) * mm, "end": v(31.2, 33.2) * mm});
            skLineSegment(sketch, "E778.0.13", {"start": v(31.2, 48.2) * mm, "end": v(31.2, 48.2) * mm});
            skLineSegment(sketch, "E778.0.14", {"start": v(31.2, 48.2) * mm, "end": v(31.2, 75) * mm});
            skLineSegment(sketch, "E778.0.15", {"start": v(31.2, 75) * mm, "end": v(31.2, 75) * mm});
            skLineSegment(sketch, "E778.0.17", {"start": v(86.2, 63) * mm, "end": v(83, 63) * mm});
            skLineSegment(sketch, "E778.0.18", {"start": v(83, 63) * mm, "end": v(83, 51) * mm});
            skLineSegment(sketch, "E778.0.19", {"start": v(83, 51) * mm, "end": v(86.2, 51) * mm});
            skLineSegment(sketch, "E779.0", {"start": v(73.8, 65.4) * mm, "end": v(59.5, 46.71) * mm});
            skArc(sketch, "E780.0", {"start": v(59.5, 46.71) * mm, "mid": v(58.7, 46.32) * mm, "end": v(57.9, 46.71) * mm});
            skLineSegment(sketch, "E781.0", {"start": v(43.6, 65.4) * mm, "end": v(57.9, 46.71) * mm});
            skArc(sketch, "E782.0", {"start": v(43.6, 65.4) * mm, "mid": v(43.5, 66.44) * mm, "end": v(44.4, 67) * mm});
            skLineSegment(sketch, "E783.0", {"start": v(73, 67) * mm, "end": v(44.4, 67) * mm});
            skArc(sketch, "E784.0", {"start": v(73, 67) * mm, "mid": v(73.9, 66.44) * mm, "end": v(73.8, 65.4) * mm});
            skLineSegment(sketch, "E785.0", {"start": v(74.2, 52.76) * mm, "end": v(64.2, 39.7) * mm});
            skLineSegment(sketch, "E786.0", {"start": v(76, 52.16) * mm, "end": v(76, 26.04) * mm});
            skArc(sketch, "E787.0", {"start": v(74.2, 52.76) * mm, "mid": v(75.32, 53.1) * mm, "end": v(76, 52.16) * mm});
            skArc(sketch, "E788.0", {"start": v(64.2, 38.5) * mm, "mid": v(64, 39.1) * mm, "end": v(64.2, 39.7) * mm});
            skLineSegment(sketch, "E789.0", {"start": v(64.2, 38.5) * mm, "end": v(74.2, 25.44) * mm});
            skArc(sketch, "E790.0", {"start": v(76, 26.04) * mm, "mid": v(75.32, 25.1) * mm, "end": v(74.2, 25.44) * mm});
            skLineSegment(sketch, "E791.0", {"start": v(53.2, 38.5) * mm, "end": v(40, 21.26) * mm});
            skArc(sketch, "E792.0", {"start": v(40, 21.26) * mm, "mid": v(38.88, 20.92) * mm, "end": v(38.2, 21.87) * mm});
            skLineSegment(sketch, "E793.0", {"start": v(38.2, 56.33) * mm, "end": v(38.2, 21.87) * mm});
            skArc(sketch, "E794.0", {"start": v(38.2, 56.33) * mm, "mid": v(38.88, 57.28) * mm, "end": v(40, 56.94) * mm});
            skLineSegment(sketch, "E795.0", {"start": v(40, 56.94) * mm, "end": v(53.2, 39.7) * mm});
            skArc(sketch, "E796.0", {"start": v(53.2, 39.7) * mm, "mid": v(53.4, 39.1) * mm, "end": v(53.2, 38.5) * mm});
            skArc(sketch, "E797.0", {"start": v(57.9, 31.49) * mm, "mid": v(58.7, 31.88) * mm, "end": v(59.5, 31.49) * mm});
            skLineSegment(sketch, "E798.0", {"start": v(57.9, 31.49) * mm, "end": v(42.83, 11.8) * mm});
            skLineSegment(sketch, "E799.0", {"start": v(59.5, 31.49) * mm, "end": v(74.57, 11.8) * mm});
            skArc(sketch, "E800.0", {"start": v(74.57, 11.8) * mm, "mid": v(74.67, 10.76) * mm, "end": v(73.77, 10.2) * mm});
            skLineSegment(sketch, "E801.0", {"start": v(73.77, 10.2) * mm, "end": v(43.63, 10.2) * mm});
            skArc(sketch, "E802.0", {"start": v(43.63, 10.2) * mm, "mid": v(42.73, 10.76) * mm, "end": v(42.83, 11.8) * mm});
            skLineSegment(sketch, "E803.0", {"start": v(89.4, 53.22) * mm, "end": v(91.2, 28.3) * mm});
            skArc(sketch, "E804.0", {"start": v(86.4, 56) * mm, "mid": v(88.45, 55.2) * mm, "end": v(89.4, 53.22) * mm});
            skLineSegment(sketch, "E805.0", {"start": v(86.2, 51) * mm, "end": v(86.2, 56) * mm});
            skLineSegment(sketch, "E806.0", {"start": v(86.2, 56) * mm, "end": v(86.4, 56) * mm});
            skLineSegment(sketch, "E807.0", {"start": v(91.2, 28.1) * mm, "end": v(91.2, 3.2) * mm});
            skLineSegment(sketch, "E808.0", {"start": v(86.2, 9) * mm, "end": v(83, 9) * mm});
            skLineSegment(sketch, "E809.0", {"start": v(86.2, 9) * mm, "end": v(86.2, 21) * mm});
            skLineSegment(sketch, "E810", {"start": v(71.2, 3.2) * mm, "end": v(91.2, 3.2) * mm});
            skArc(sketch, "E811.0", {"start": v(91.2, 28.3) * mm, "mid": v(91.2, 28.2) * mm, "end": v(91.2, 28.1) * mm});
            skLineSegment(sketch, "E812.0", {"start": v(31.2, 75) * mm, "end": v(76.2, 75) * mm});
            skArc(sketch, "E813.0", {"start": v(76.2, 75) * mm, "mid": v(83.27, 72.07) * mm, "end": v(86.2, 65) * mm});
            skLineSegment(sketch, "E814.0", {"start": v(86.2, 63) * mm, "end": v(86.2, 65) * mm});
            skLineSegment(sketch, "E815.0", {"start": v(26.5, 48.2) * mm, "end": v(31.2, 48.2) * mm});
            skArc(sketch, "E816.0", {"start": v(24, 45.7) * mm, "mid": v(24.73, 47.47) * mm, "end": v(26.5, 48.2) * mm});
            skLineSegment(sketch, "E817.0", {"start": v(24, 35.7) * mm, "end": v(24, 45.7) * mm});
            skArc(sketch, "E818.0", {"start": v(26.5, 33.2) * mm, "mid": v(24.73, 33.93) * mm, "end": v(24, 35.7) * mm});
            skLineSegment(sketch, "E819.0", {"start": v(31.2, 33.2) * mm, "end": v(26.5, 33.2) * mm});
            skLineSegment(sketch, "E820.0", {"start": v(26.5, 44.7) * mm, "end": v(26.5, 36.7) * mm});
            skArc(sketch, "E821.0", {"start": v(28.5, 44.7) * mm, "mid": v(27.5, 45.7) * mm, "end": v(26.5, 44.7) * mm});
            skLineSegment(sketch, "E822.0", {"start": v(28.5, 44.7) * mm, "end": v(28.5, 36.7) * mm});
            skArc(sketch, "E823.0", {"start": v(26.5, 36.7) * mm, "mid": v(27.5, 35.7) * mm, "end": v(28.5, 36.7) * mm});
            skSolve(sketch);
        }
        {
            var Q0;
            Q0 = qSketchRegion(id + "F33", true);
            extrude(context, id + "F34", {"entities" : qUnion([Q0]), "oppositeDirection" : true, "depth" : 3.2 * mm});
        }
        {
            var Q0;
            Q0=makeQuery(id+"F30.opExtrude","CAP_VERTEX",VERTEX,{"disambiguationData":[OSD([sQuery(id+"F29.wireOp",EDGE,"E755"),sQuery(id+"F29.wireOp",EDGE,"E756")])],"isStart":false});
            var Q1;
            Q1=makeQuery(id+"F30.opExtrude","CAP_VERTEX",VERTEX,{"disambiguationData":[OSD([sQuery(id+"F29.wireOp",EDGE,"E727"),sQuery(id+"F29.wireOp",EDGE,"E760")])],"isStart":false});
            var Q2;
            Q2=makeQuery(id+"F34.opExtrude","CAP_VERTEX",VERTEX,{"disambiguationData":[OSD([sQuery(id+"F33.wireOp",EDGE,"E808.0"),sQuery(id+"F33.wireOp",EDGE,"E809.0")])],"isStart":true});
            cPlane(context, id + "F35", {"entities" : qUnion([Q0, Q1, Q2]), "cplaneType" : CPlaneType.THREE_POINT, "offset" : 25 * mm, "width" : 150 * mm, "height" : 150 * mm});
        }
        {
            var Q0;
            Q0=qCreatedBy(id+"F35.planeOp",FACE);
            var sketch = newSketch(context, id + "F36", { "sketchPlane" : qUnion([Q0])});
            skLineSegment(sketch, "E824.0", {"start": v(36.7, 63) * mm, "end": v(-39.7, 63) * mm});
            skLineSegment(sketch, "E825.0", {"start": v(36.7, 51) * mm, "end": v(33.5, 51) * mm});
            skLineSegment(sketch, "E826.0", {"start": v(36.7, 51) * mm, "end": v(36.7, 63) * mm});
            skLineSegment(sketch, "E827.0", {"start": v(33.5, 21) * mm, "end": v(33.5, 51) * mm});
            skLineSegment(sketch, "E828.0", {"start": v(36.7, 21) * mm, "end": v(33.5, 21) * mm});
            skLineSegment(sketch, "E829.0", {"start": v(36.7, 9) * mm, "end": v(36.7, 21) * mm});
            skLineSegment(sketch, "E830.0", {"start": v(33.5, 9) * mm, "end": v(36.7, 9) * mm});
            skLineSegment(sketch, "E831.0", {"start": v(33.5, 0) * mm, "end": v(33.5, 9) * mm});
            skLineSegment(sketch, "E832.0", {"start": v(-36.5, 9) * mm, "end": v(-36.5, 0) * mm});
            skLineSegment(sketch, "E833.0", {"start": v(-39.7, 9) * mm, "end": v(-36.5, 9) * mm});
            skLineSegment(sketch, "E834.0", {"start": v(-39.7, 21) * mm, "end": v(-39.7, 21) * mm});
            skLineSegment(sketch, "E835.0", {"start": v(-39.7, 21) * mm, "end": v(-36.5, 21) * mm});
            skLineSegment(sketch, "E836.0", {"start": v(-36.5, 51) * mm, "end": v(-36.5, 21) * mm});
            skLineSegment(sketch, "E837.0", {"start": v(-39.7, 51) * mm, "end": v(-36.5, 51) * mm});
            skLineSegment(sketch, "E838.0", {"start": v(-39.7, 63) * mm, "end": v(-39.7, 51) * mm});
            skLineSegment(sketch, "E839", {"start": v(33.5, 0) * mm, "end": v(-36.5, 0) * mm});
            skPoint(sketch, "E840.0", {"position": v(-36.5, 63) * mm});
            skPoint(sketch, "E841.0", {"position": v(33.5, 63) * mm});
            skLineSegment(sketch, "E842", {"start": v(33.5, 63) * mm, "end": v(-36.5, 0) * mm, "construction": true});
            skLineSegment(sketch, "E843", {"start": v(-36.5, 63) * mm, "end": v(33.5, 0) * mm, "construction": true});
            skLineSegment(sketch, "E844.0", {"start": v(23.83, 48.92) * mm, "end": v(5.3, 32.24) * mm});
            skLineSegment(sketch, "E845.0", {"start": v(-26.83, 48.92) * mm, "end": v(-8.3, 32.24) * mm});
            skLineSegment(sketch, "E846", {"start": v(-28.5, 48.17) * mm, "end": v(-28.5, 14.83) * mm});
            skLineSegment(sketch, "E847", {"start": v(16.03, 55) * mm, "end": v(-19.03, 55) * mm});
            skLineSegment(sketch, "E848", {"start": v(25.5, 48.17) * mm, "end": v(25.5, 14.83) * mm});
            skLineSegment(sketch, "E849", {"start": v(16.03, 8) * mm, "end": v(-19.03, 8) * mm});
            skLineSegment(sketch, "E850.trimOffspring", {"start": v(16.7, 53.26) * mm, "end": v(-0.83, 37.48) * mm});
            skLineSegment(sketch, "E851.trimOffspring", {"start": v(-19.7, 53.26) * mm, "end": v(-2.17, 37.48) * mm});
            skLineSegment(sketch, "E852.trimOffspring", {"start": v(-0.83, 25.52) * mm, "end": v(16.7, 9.74) * mm});
            skLineSegment(sketch, "E853.trimOffspring", {"start": v(5.3, 30.76) * mm, "end": v(23.83, 14.08) * mm});
            skLineSegment(sketch, "E854.trimOffspring", {"start": v(-2.17, 25.52) * mm, "end": v(-19.7, 9.74) * mm});
            skLineSegment(sketch, "E855.trimOffspring", {"start": v(-8.3, 30.76) * mm, "end": v(-26.83, 14.08) * mm});
            skPoint(sketch, "E856.visualSharp", {"position": v(25.5, 50.42) * mm});
            skArc(sketch, "E856.filletArc", {"start": v(25.5, 48.17) * mm, "mid": v(24.9, 49.09) * mm, "end": v(23.83, 48.92) * mm});
            skPoint(sketch, "E857.visualSharp", {"position": v(18.63, 8) * mm});
            skArc(sketch, "E857.filletArc", {"start": v(16.03, 8) * mm, "mid": v(16.96, 8.64) * mm, "end": v(16.7, 9.74) * mm});
            skPoint(sketch, "E858.visualSharp", {"position": v(-1.5, 26.12) * mm});
            skArc(sketch, "E858.filletArc", {"start": v(-0.83, 25.52) * mm, "mid": v(-1.5, 25.77) * mm, "end": v(-2.17, 25.52) * mm});
            skPoint(sketch, "E859.visualSharp", {"position": v(-21.63, 8) * mm});
            skArc(sketch, "E859.filletArc", {"start": v(-19.7, 9.74) * mm, "mid": v(-19.96, 8.64) * mm, "end": v(-19.03, 8) * mm});
            skPoint(sketch, "E860.visualSharp", {"position": v(-28.5, 12.58) * mm});
            skArc(sketch, "E860.filletArc", {"start": v(-28.5, 14.83) * mm, "mid": v(-27.9, 13.91) * mm, "end": v(-26.83, 14.08) * mm});
            skPoint(sketch, "E861.visualSharp", {"position": v(-28.5, 50.42) * mm});
            skArc(sketch, "E861.filletArc", {"start": v(-26.83, 48.92) * mm, "mid": v(-27.9, 49.09) * mm, "end": v(-28.5, 48.17) * mm});
            skPoint(sketch, "E862.visualSharp", {"position": v(-7.48, 31.5) * mm});
            skArc(sketch, "E862.filletArc", {"start": v(-8.3, 30.76) * mm, "mid": v(-7.97, 31.5) * mm, "end": v(-8.3, 32.24) * mm});
            skPoint(sketch, "E863.visualSharp", {"position": v(-21.63, 55) * mm});
            skArc(sketch, "E863.filletArc", {"start": v(-19.03, 55) * mm, "mid": v(-19.96, 54.36) * mm, "end": v(-19.7, 53.26) * mm});
            skPoint(sketch, "E864.visualSharp", {"position": v(18.63, 55) * mm});
            skArc(sketch, "E864.filletArc", {"start": v(16.7, 53.26) * mm, "mid": v(16.96, 54.36) * mm, "end": v(16.03, 55) * mm});
            skPoint(sketch, "E865.visualSharp", {"position": v(-1.5, 36.88) * mm});
            skArc(sketch, "E865.filletArc", {"start": v(-2.17, 37.48) * mm, "mid": v(-1.5, 37.23) * mm, "end": v(-0.83, 37.48) * mm});
            skPoint(sketch, "E866.visualSharp", {"position": v(4.48, 31.5) * mm});
            skArc(sketch, "E866.filletArc", {"start": v(5.3, 32.24) * mm, "mid": v(4.97, 31.5) * mm, "end": v(5.3, 30.76) * mm});
            skPoint(sketch, "E867.visualSharp", {"position": v(25.5, 12.58) * mm});
            skArc(sketch, "E867.filletArc", {"start": v(23.83, 14.08) * mm, "mid": v(24.9, 13.91) * mm, "end": v(25.5, 14.83) * mm});
            skLineSegment(sketch, "E868", {"start": v(-39.7, 21) * mm, "end": v(-39.7, 9) * mm});
            skPoint(sketch, "E869.0", {"position": v(-39.7, 9) * mm});
            skPoint(sketch, "E870.0", {"position": v(-36.5, 9) * mm});
            skPoint(sketch, "E871.0", {"position": v(-36.5, 0) * mm});
            skPoint(sketch, "E872.0", {"position": v(33.5, 0) * mm});
            skPoint(sketch, "E873.0", {"position": v(33.5, 21) * mm});
            skPoint(sketch, "E874.0", {"position": v(-36.5, 51) * mm});
            skSolve(sketch);
        }
        {
            var Q0;
            Q0 = qSketchRegion(id + "F36", true);
            extrude(context, id + "F37", {"entities" : qUnion([Q0]), "depth" : 3.2 * mm});
        }
        {
            var Q0;
            Q0=qCreatedBy(makeId("Front.planeOp"),FACE);
            var sketch = newSketch(context, id + "F38", { "sketchPlane" : qUnion([Q0])});
            skLineSegment(sketch, "E875.bottom", {"start": v(-109.5, 0) * mm, "end": v(-70, 0) * mm, "construction": true});
            skLineSegment(sketch, "E875.top", {"start": v(-110, 175.5) * mm, "end": v(-70, 175.5) * mm, "construction": true});
            skLineSegment(sketch, "E875.left", {"start": v(-110, 0) * mm, "end": v(-110, 175.5) * mm, "construction": true});
            skLineSegment(sketch, "E875.right", {"start": v(-70, 0) * mm, "end": v(-70, 175.5) * mm, "construction": true});
            skLineSegment(sketch, "E876.0", {"start": v(-110, 0) * mm, "end": v(110, 0) * mm, "construction": true});
            skLineSegment(sketch, "E877", {"start": v(-110, 0) * mm, "end": v(-110, 115.55) * mm});
            skFitSpline(sketch, "E878", {"points": [v(-110, 115.55) * mm, v(-83.7, 175.5) * mm, v(-70, 167.74) * mm], "startDerivative": vector(0, 244.54) * mm, "endDerivative": vector(36.14, -70.77) * mm});
            skFitSpline(sketch, "E879.0", {"points": [v(-109.5, 115.55) * mm, v(-109.5, 125.72) * mm, v(-108.44, 142.56) * mm, v(-105.1, 156.37) * mm, v(-101.63, 163.97) * mm, v(-98.73, 168.17) * mm, v(-95.63, 171.12) * mm, v(-92.41, 173.06) * mm, v(-89.7, 174.02) * mm, v(-87.54, 174.52) * mm, v(-85.94, 174.78) * mm, v(-84.38, 174.95) * mm, v(-82.86, 175.07) * mm, v(-81.4, 175.13) * mm, v(-79.55, 175.08) * mm, v(-77.4, 174.7) * mm, v(-75, 173.53) * mm, v(-72.69, 171.32) * mm, v(-71.19, 168.96) * mm, v(-70.45, 167.5) * mm]});
            skLineSegment(sketch, "E879.1", {"start": v(-109.5, 0) * mm, "end": v(-109.5, 115.55) * mm});
            skLineSegment(sketch, "E880", {"start": v(-70.45, 167.5) * mm, "end": v(-70, 167.74) * mm});
            skLineSegment(sketch, "E881", {"start": v(-110, 0) * mm, "end": v(-109.5, 0) * mm});
            skLineSegment(sketch, "E882", {"start": v(0, 0) * mm, "end": v(0, 310.06) * mm, "construction": true});
            skSolve(sketch);
        }
        {
            var Q0;
            Q0 = qSketchRegion(id + "F38", true);
            var Q1;
            Q1=sQuery(id+"F38.wireOp",EDGE,"E882");
            revolve(context, id + "F39", {"entities" : qUnion([Q0]), "axis" : qUnion([Q1]), "revolveType" : RevolveType.FULL});
        }
    });
